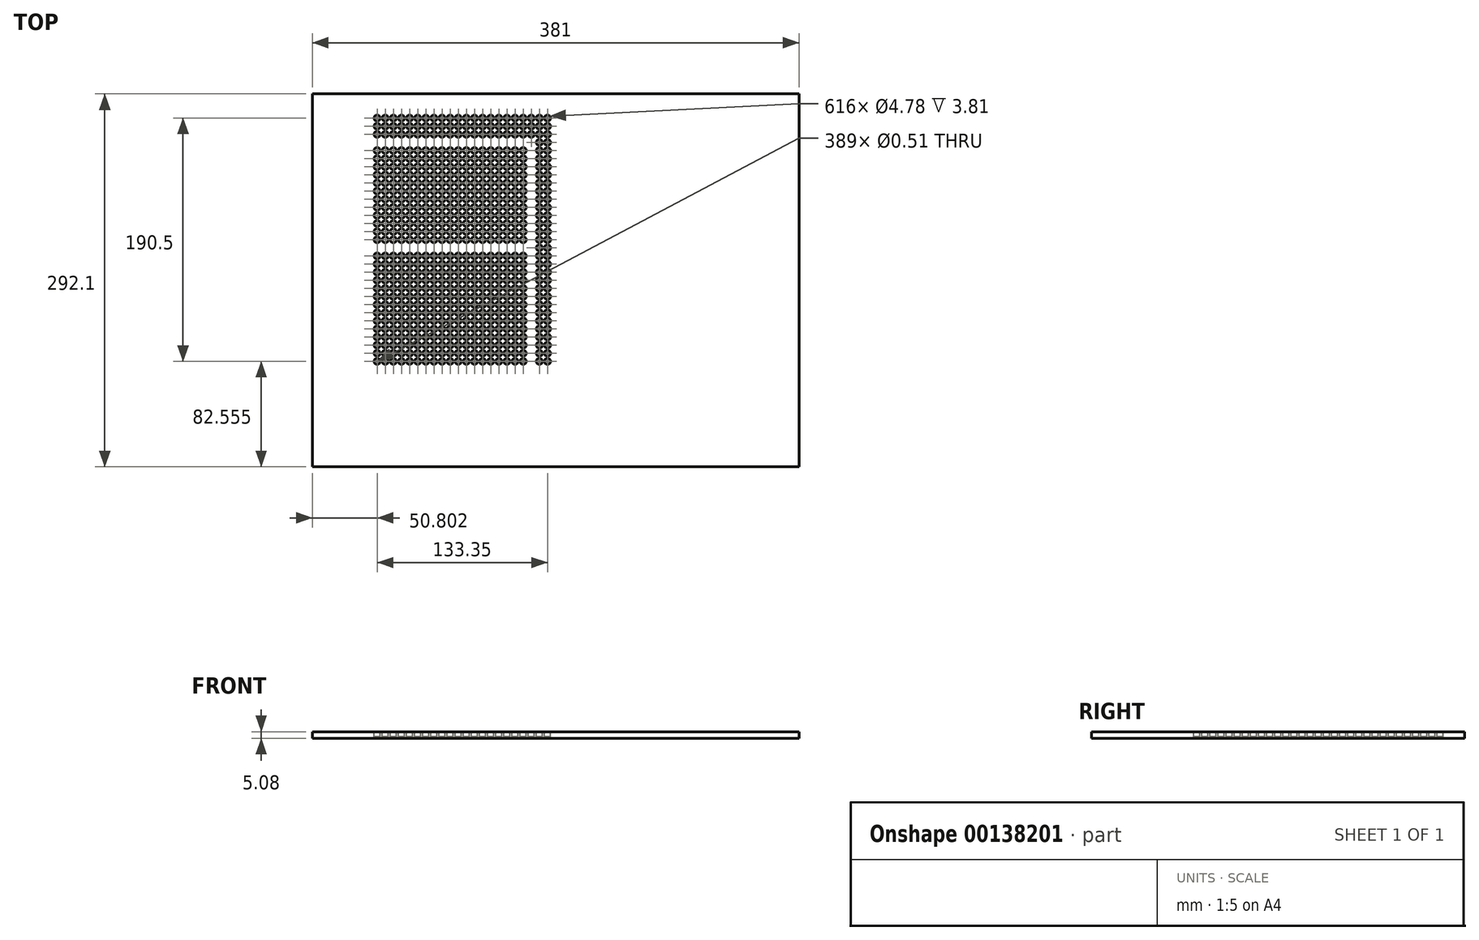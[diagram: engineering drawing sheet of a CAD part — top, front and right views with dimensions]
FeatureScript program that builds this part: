
annotation { "Feature Type Name" : "Feature", "Feature Type Description" : "" }
export const myFeature = defineFeature(function(context is Context, id is Id, definition is map)
    precondition{}
    {
        {
            var Q0;
            Q0=qCreatedBy(makeId("Top.planeOp"),FACE);
            var sketch = newSketch(context, id + "F0", { "sketchPlane" : qUnion([Q0])});
            skLineSegment(sketch, "E0.bottom", {"start": v(-148.53, -103.2) * mm, "end": v(232.47, -103.2) * mm});
            skLineSegment(sketch, "E0.top", {"start": v(-148.53, 188.9) * mm, "end": v(232.47, 188.9) * mm});
            skLineSegment(sketch, "E0.left", {"start": v(-148.53, -103.2) * mm, "end": v(-148.53, 188.9) * mm});
            skLineSegment(sketch, "E0.right", {"start": v(232.47, -103.2) * mm, "end": v(232.47, 188.9) * mm});
            skSolve(sketch);
        }
        {
            var Q0;
            Q0 = qSketchRegion(id + "F0", true);
            extrude(context, id + "F1", {"entities" : qUnion([Q0]), "depth" : 5.08 * mm});
        }
        {
            var Q0;
            Q0=makeQuery(id+"F1.opExtrude","CAP_FACE",FACE,{"disambiguationData":[OSD([sQuery(id+"F0.wireOp",EDGE,"E0.bottom"),sQuery(id+"F0.wireOp",EDGE,"E0.top"),sQuery(id+"F0.wireOp",EDGE,"E0.left"),sQuery(id+"F0.wireOp",EDGE,"E0.right")])],"isStart":false});
            var sketch = newSketch(context, id + "F2", { "sketchPlane" : qUnion([Q0])});
            skCircle(sketch, "E1", {"center": v(-97.73, -20.65) * mm, "radius": 2.39 * mm});
            skCircle(sketch, "E2.0.1.0", {"center": v(-97.73, -14.3) * mm, "radius": 2.39 * mm});
            skCircle(sketch, "E2.0.2.0", {"center": v(-97.73, -7.95) * mm, "radius": 2.39 * mm});
            skCircle(sketch, "E2.0.3.0", {"center": v(-97.73, -1.6) * mm, "radius": 2.39 * mm});
            skCircle(sketch, "E2.0.4.0", {"center": v(-97.73, 4.75) * mm, "radius": 2.39 * mm});
            skCircle(sketch, "E2.0.5.0", {"center": v(-97.73, 11.1) * mm, "radius": 2.39 * mm});
            skCircle(sketch, "E2.0.6.0", {"center": v(-97.73, 17.45) * mm, "radius": 2.39 * mm});
            skCircle(sketch, "E2.0.7.0", {"center": v(-97.73, 23.8) * mm, "radius": 2.39 * mm});
            skCircle(sketch, "E2.0.8.0", {"center": v(-97.73, 30.15) * mm, "radius": 2.39 * mm});
            skCircle(sketch, "E2.0.9.0", {"center": v(-97.73, 36.5) * mm, "radius": 2.39 * mm});
            skCircle(sketch, "E2.0.10.0", {"center": v(-97.73, 42.85) * mm, "radius": 2.39 * mm});
            skCircle(sketch, "E2.0.11.0", {"center": v(-97.73, 49.2) * mm, "radius": 2.39 * mm});
            skCircle(sketch, "E2.0.12.0", {"center": v(-97.73, 55.55) * mm, "radius": 2.39 * mm});
            skCircle(sketch, "E2.0.13.0", {"center": v(-97.73, 61.9) * mm, "radius": 2.39 * mm});
            skCircle(sketch, "E2.1.0.0", {"center": v(-91.38, -20.65) * mm, "radius": 2.39 * mm});
            skCircle(sketch, "E2.1.1.0", {"center": v(-91.38, -14.3) * mm, "radius": 2.39 * mm});
            skCircle(sketch, "E2.1.2.0", {"center": v(-91.38, -7.95) * mm, "radius": 2.39 * mm});
            skCircle(sketch, "E2.1.3.0", {"center": v(-91.38, -1.6) * mm, "radius": 2.39 * mm});
            skCircle(sketch, "E2.1.4.0", {"center": v(-91.38, 4.75) * mm, "radius": 2.39 * mm});
            skCircle(sketch, "E2.1.5.0", {"center": v(-91.38, 11.1) * mm, "radius": 2.39 * mm});
            skCircle(sketch, "E2.1.6.0", {"center": v(-91.38, 17.45) * mm, "radius": 2.39 * mm});
            skCircle(sketch, "E2.1.7.0", {"center": v(-91.38, 23.8) * mm, "radius": 2.39 * mm});
            skCircle(sketch, "E2.1.8.0", {"center": v(-91.38, 30.15) * mm, "radius": 2.39 * mm});
            skCircle(sketch, "E2.1.9.0", {"center": v(-91.38, 36.5) * mm, "radius": 2.39 * mm});
            skCircle(sketch, "E2.1.10.0", {"center": v(-91.38, 42.85) * mm, "radius": 2.39 * mm});
            skCircle(sketch, "E2.1.11.0", {"center": v(-91.38, 49.2) * mm, "radius": 2.39 * mm});
            skCircle(sketch, "E2.1.12.0", {"center": v(-91.38, 55.55) * mm, "radius": 2.39 * mm});
            skCircle(sketch, "E2.1.13.0", {"center": v(-91.38, 61.9) * mm, "radius": 2.39 * mm});
            skCircle(sketch, "E2.2.0.0", {"center": v(-85.03, -20.65) * mm, "radius": 2.39 * mm});
            skCircle(sketch, "E2.2.1.0", {"center": v(-85.03, -14.3) * mm, "radius": 2.39 * mm});
            skCircle(sketch, "E2.2.2.0", {"center": v(-85.03, -7.95) * mm, "radius": 2.39 * mm});
            skCircle(sketch, "E2.2.3.0", {"center": v(-85.03, -1.6) * mm, "radius": 2.39 * mm});
            skCircle(sketch, "E2.2.4.0", {"center": v(-85.03, 4.75) * mm, "radius": 2.39 * mm});
            skCircle(sketch, "E2.2.5.0", {"center": v(-85.03, 11.1) * mm, "radius": 2.39 * mm});
            skCircle(sketch, "E2.2.6.0", {"center": v(-85.03, 17.45) * mm, "radius": 2.39 * mm});
            skCircle(sketch, "E2.2.7.0", {"center": v(-85.03, 23.8) * mm, "radius": 2.39 * mm});
            skCircle(sketch, "E2.2.8.0", {"center": v(-85.03, 30.15) * mm, "radius": 2.39 * mm});
            skCircle(sketch, "E2.2.9.0", {"center": v(-85.03, 36.5) * mm, "radius": 2.39 * mm});
            skCircle(sketch, "E2.2.10.0", {"center": v(-85.03, 42.85) * mm, "radius": 2.39 * mm});
            skCircle(sketch, "E2.2.11.0", {"center": v(-85.03, 49.2) * mm, "radius": 2.39 * mm});
            skCircle(sketch, "E2.2.12.0", {"center": v(-85.03, 55.55) * mm, "radius": 2.39 * mm});
            skCircle(sketch, "E2.2.13.0", {"center": v(-85.03, 61.9) * mm, "radius": 2.39 * mm});
            skCircle(sketch, "E2.3.0.0", {"center": v(-78.68, -20.65) * mm, "radius": 2.39 * mm});
            skCircle(sketch, "E2.3.1.0", {"center": v(-78.68, -14.3) * mm, "radius": 2.39 * mm});
            skCircle(sketch, "E2.3.2.0", {"center": v(-78.68, -7.95) * mm, "radius": 2.39 * mm});
            skCircle(sketch, "E2.3.3.0", {"center": v(-78.68, -1.6) * mm, "radius": 2.39 * mm});
            skCircle(sketch, "E2.3.4.0", {"center": v(-78.68, 4.75) * mm, "radius": 2.39 * mm});
            skCircle(sketch, "E2.3.5.0", {"center": v(-78.68, 11.1) * mm, "radius": 2.39 * mm});
            skCircle(sketch, "E2.3.6.0", {"center": v(-78.68, 17.45) * mm, "radius": 2.39 * mm});
            skCircle(sketch, "E2.3.7.0", {"center": v(-78.68, 23.8) * mm, "radius": 2.39 * mm});
            skCircle(sketch, "E2.3.8.0", {"center": v(-78.68, 30.15) * mm, "radius": 2.39 * mm});
            skCircle(sketch, "E2.3.9.0", {"center": v(-78.68, 36.5) * mm, "radius": 2.39 * mm});
            skCircle(sketch, "E2.3.10.0", {"center": v(-78.68, 42.85) * mm, "radius": 2.39 * mm});
            skCircle(sketch, "E2.3.11.0", {"center": v(-78.68, 49.2) * mm, "radius": 2.39 * mm});
            skCircle(sketch, "E2.3.12.0", {"center": v(-78.68, 55.55) * mm, "radius": 2.39 * mm});
            skCircle(sketch, "E2.3.13.0", {"center": v(-78.68, 61.9) * mm, "radius": 2.39 * mm});
            skCircle(sketch, "E2.4.0.0", {"center": v(-72.33, -20.65) * mm, "radius": 2.39 * mm});
            skCircle(sketch, "E2.4.1.0", {"center": v(-72.33, -14.3) * mm, "radius": 2.39 * mm});
            skCircle(sketch, "E2.4.2.0", {"center": v(-72.33, -7.95) * mm, "radius": 2.39 * mm});
            skCircle(sketch, "E2.4.3.0", {"center": v(-72.33, -1.6) * mm, "radius": 2.39 * mm});
            skCircle(sketch, "E2.4.4.0", {"center": v(-72.33, 4.75) * mm, "radius": 2.39 * mm});
            skCircle(sketch, "E2.4.5.0", {"center": v(-72.33, 11.1) * mm, "radius": 2.39 * mm});
            skCircle(sketch, "E2.4.6.0", {"center": v(-72.33, 17.45) * mm, "radius": 2.39 * mm});
            skCircle(sketch, "E2.4.7.0", {"center": v(-72.33, 23.8) * mm, "radius": 2.39 * mm});
            skCircle(sketch, "E2.4.8.0", {"center": v(-72.33, 30.15) * mm, "radius": 2.39 * mm});
            skCircle(sketch, "E2.4.9.0", {"center": v(-72.33, 36.5) * mm, "radius": 2.39 * mm});
            skCircle(sketch, "E2.4.10.0", {"center": v(-72.33, 42.85) * mm, "radius": 2.39 * mm});
            skCircle(sketch, "E2.4.11.0", {"center": v(-72.33, 49.2) * mm, "radius": 2.39 * mm});
            skCircle(sketch, "E2.4.12.0", {"center": v(-72.33, 55.55) * mm, "radius": 2.39 * mm});
            skCircle(sketch, "E2.4.13.0", {"center": v(-72.33, 61.9) * mm, "radius": 2.39 * mm});
            skCircle(sketch, "E2.5.0.0", {"center": v(-65.98, -20.65) * mm, "radius": 2.39 * mm});
            skCircle(sketch, "E2.5.1.0", {"center": v(-65.98, -14.3) * mm, "radius": 2.39 * mm});
            skCircle(sketch, "E2.5.2.0", {"center": v(-65.98, -7.95) * mm, "radius": 2.39 * mm});
            skCircle(sketch, "E2.5.3.0", {"center": v(-65.98, -1.6) * mm, "radius": 2.39 * mm});
            skCircle(sketch, "E2.5.4.0", {"center": v(-65.98, 4.75) * mm, "radius": 2.39 * mm});
            skCircle(sketch, "E2.5.5.0", {"center": v(-65.98, 11.1) * mm, "radius": 2.39 * mm});
            skCircle(sketch, "E2.5.6.0", {"center": v(-65.98, 17.45) * mm, "radius": 2.39 * mm});
            skCircle(sketch, "E2.5.7.0", {"center": v(-65.98, 23.8) * mm, "radius": 2.39 * mm});
            skCircle(sketch, "E2.5.8.0", {"center": v(-65.98, 30.15) * mm, "radius": 2.39 * mm});
            skCircle(sketch, "E2.5.9.0", {"center": v(-65.98, 36.5) * mm, "radius": 2.39 * mm});
            skCircle(sketch, "E2.5.10.0", {"center": v(-65.98, 42.85) * mm, "radius": 2.39 * mm});
            skCircle(sketch, "E2.5.11.0", {"center": v(-65.98, 49.2) * mm, "radius": 2.39 * mm});
            skCircle(sketch, "E2.5.12.0", {"center": v(-65.98, 55.55) * mm, "radius": 2.39 * mm});
            skCircle(sketch, "E2.5.13.0", {"center": v(-65.98, 61.9) * mm, "radius": 2.39 * mm});
            skCircle(sketch, "E2.6.0.0", {"center": v(-59.63, -20.65) * mm, "radius": 2.39 * mm});
            skCircle(sketch, "E2.6.1.0", {"center": v(-59.63, -14.3) * mm, "radius": 2.39 * mm});
            skCircle(sketch, "E2.6.2.0", {"center": v(-59.63, -7.95) * mm, "radius": 2.39 * mm});
            skCircle(sketch, "E2.6.3.0", {"center": v(-59.63, -1.6) * mm, "radius": 2.39 * mm});
            skCircle(sketch, "E2.6.4.0", {"center": v(-59.63, 4.75) * mm, "radius": 2.39 * mm});
            skCircle(sketch, "E2.6.5.0", {"center": v(-59.63, 11.1) * mm, "radius": 2.39 * mm});
            skCircle(sketch, "E2.6.6.0", {"center": v(-59.63, 17.45) * mm, "radius": 2.39 * mm});
            skCircle(sketch, "E2.6.7.0", {"center": v(-59.63, 23.8) * mm, "radius": 2.39 * mm});
            skCircle(sketch, "E2.6.8.0", {"center": v(-59.63, 30.15) * mm, "radius": 2.39 * mm});
            skCircle(sketch, "E2.6.9.0", {"center": v(-59.63, 36.5) * mm, "radius": 2.39 * mm});
            skCircle(sketch, "E2.6.10.0", {"center": v(-59.63, 42.85) * mm, "radius": 2.39 * mm});
            skCircle(sketch, "E2.6.11.0", {"center": v(-59.63, 49.2) * mm, "radius": 2.39 * mm});
            skCircle(sketch, "E2.6.12.0", {"center": v(-59.63, 55.55) * mm, "radius": 2.39 * mm});
            skCircle(sketch, "E2.6.13.0", {"center": v(-59.63, 61.9) * mm, "radius": 2.39 * mm});
            skCircle(sketch, "E2.7.0.0", {"center": v(-53.28, -20.65) * mm, "radius": 2.39 * mm});
            skCircle(sketch, "E2.7.1.0", {"center": v(-53.28, -14.3) * mm, "radius": 2.39 * mm});
            skCircle(sketch, "E2.7.2.0", {"center": v(-53.28, -7.95) * mm, "radius": 2.39 * mm});
            skCircle(sketch, "E2.7.3.0", {"center": v(-53.28, -1.6) * mm, "radius": 2.39 * mm});
            skCircle(sketch, "E2.7.4.0", {"center": v(-53.28, 4.75) * mm, "radius": 2.39 * mm});
            skCircle(sketch, "E2.7.5.0", {"center": v(-53.28, 11.1) * mm, "radius": 2.39 * mm});
            skCircle(sketch, "E2.7.6.0", {"center": v(-53.28, 17.45) * mm, "radius": 2.39 * mm});
            skCircle(sketch, "E2.7.7.0", {"center": v(-53.28, 23.8) * mm, "radius": 2.39 * mm});
            skCircle(sketch, "E2.7.8.0", {"center": v(-53.28, 30.15) * mm, "radius": 2.39 * mm});
            skCircle(sketch, "E2.7.9.0", {"center": v(-53.28, 36.5) * mm, "radius": 2.39 * mm});
            skCircle(sketch, "E2.7.10.0", {"center": v(-53.28, 42.85) * mm, "radius": 2.39 * mm});
            skCircle(sketch, "E2.7.11.0", {"center": v(-53.28, 49.2) * mm, "radius": 2.39 * mm});
            skCircle(sketch, "E2.7.12.0", {"center": v(-53.28, 55.55) * mm, "radius": 2.39 * mm});
            skCircle(sketch, "E2.7.13.0", {"center": v(-53.28, 61.9) * mm, "radius": 2.39 * mm});
            skCircle(sketch, "E2.8.0.0", {"center": v(-46.93, -20.65) * mm, "radius": 2.39 * mm});
            skCircle(sketch, "E2.8.1.0", {"center": v(-46.93, -14.3) * mm, "radius": 2.39 * mm});
            skCircle(sketch, "E2.8.2.0", {"center": v(-46.93, -7.95) * mm, "radius": 2.39 * mm});
            skCircle(sketch, "E2.8.3.0", {"center": v(-46.93, -1.6) * mm, "radius": 2.39 * mm});
            skCircle(sketch, "E2.8.4.0", {"center": v(-46.93, 4.75) * mm, "radius": 2.39 * mm});
            skCircle(sketch, "E2.8.5.0", {"center": v(-46.93, 11.1) * mm, "radius": 2.39 * mm});
            skCircle(sketch, "E2.8.6.0", {"center": v(-46.93, 17.45) * mm, "radius": 2.39 * mm});
            skCircle(sketch, "E2.8.7.0", {"center": v(-46.93, 23.8) * mm, "radius": 2.39 * mm});
            skCircle(sketch, "E2.8.8.0", {"center": v(-46.93, 30.15) * mm, "radius": 2.39 * mm});
            skCircle(sketch, "E2.8.9.0", {"center": v(-46.93, 36.5) * mm, "radius": 2.39 * mm});
            skCircle(sketch, "E2.8.10.0", {"center": v(-46.93, 42.85) * mm, "radius": 2.39 * mm});
            skCircle(sketch, "E2.8.11.0", {"center": v(-46.93, 49.2) * mm, "radius": 2.39 * mm});
            skCircle(sketch, "E2.8.12.0", {"center": v(-46.93, 55.55) * mm, "radius": 2.39 * mm});
            skCircle(sketch, "E2.8.13.0", {"center": v(-46.93, 61.9) * mm, "radius": 2.39 * mm});
            skCircle(sketch, "E2.9.0.0", {"center": v(-40.58, -20.65) * mm, "radius": 2.39 * mm});
            skCircle(sketch, "E2.9.1.0", {"center": v(-40.58, -14.3) * mm, "radius": 2.39 * mm});
            skCircle(sketch, "E2.9.2.0", {"center": v(-40.58, -7.95) * mm, "radius": 2.39 * mm});
            skCircle(sketch, "E2.9.3.0", {"center": v(-40.58, -1.6) * mm, "radius": 2.39 * mm});
            skCircle(sketch, "E2.9.4.0", {"center": v(-40.58, 4.75) * mm, "radius": 2.39 * mm});
            skCircle(sketch, "E2.9.5.0", {"center": v(-40.58, 11.1) * mm, "radius": 2.39 * mm});
            skCircle(sketch, "E2.9.6.0", {"center": v(-40.58, 17.45) * mm, "radius": 2.39 * mm});
            skCircle(sketch, "E2.9.7.0", {"center": v(-40.58, 23.8) * mm, "radius": 2.39 * mm});
            skCircle(sketch, "E2.9.8.0", {"center": v(-40.58, 30.15) * mm, "radius": 2.39 * mm});
            skCircle(sketch, "E2.9.9.0", {"center": v(-40.58, 36.5) * mm, "radius": 2.39 * mm});
            skCircle(sketch, "E2.9.10.0", {"center": v(-40.58, 42.85) * mm, "radius": 2.39 * mm});
            skCircle(sketch, "E2.9.11.0", {"center": v(-40.58, 49.2) * mm, "radius": 2.39 * mm});
            skCircle(sketch, "E2.9.12.0", {"center": v(-40.58, 55.55) * mm, "radius": 2.39 * mm});
            skCircle(sketch, "E2.9.13.0", {"center": v(-40.58, 61.9) * mm, "radius": 2.39 * mm});
            skCircle(sketch, "E2.10.0.0", {"center": v(-34.23, -20.65) * mm, "radius": 2.39 * mm});
            skCircle(sketch, "E2.10.1.0", {"center": v(-34.23, -14.3) * mm, "radius": 2.39 * mm});
            skCircle(sketch, "E2.10.2.0", {"center": v(-34.23, -7.95) * mm, "radius": 2.39 * mm});
            skCircle(sketch, "E2.10.3.0", {"center": v(-34.23, -1.6) * mm, "radius": 2.39 * mm});
            skCircle(sketch, "E2.10.4.0", {"center": v(-34.23, 4.75) * mm, "radius": 2.39 * mm});
            skCircle(sketch, "E2.10.5.0", {"center": v(-34.23, 11.1) * mm, "radius": 2.39 * mm});
            skCircle(sketch, "E2.10.6.0", {"center": v(-34.23, 17.45) * mm, "radius": 2.39 * mm});
            skCircle(sketch, "E2.10.7.0", {"center": v(-34.23, 23.8) * mm, "radius": 2.39 * mm});
            skCircle(sketch, "E2.10.8.0", {"center": v(-34.23, 30.15) * mm, "radius": 2.39 * mm});
            skCircle(sketch, "E2.10.9.0", {"center": v(-34.23, 36.5) * mm, "radius": 2.39 * mm});
            skCircle(sketch, "E2.10.10.0", {"center": v(-34.23, 42.85) * mm, "radius": 2.39 * mm});
            skCircle(sketch, "E2.10.11.0", {"center": v(-34.23, 49.2) * mm, "radius": 2.39 * mm});
            skCircle(sketch, "E2.10.12.0", {"center": v(-34.23, 55.55) * mm, "radius": 2.39 * mm});
            skCircle(sketch, "E2.10.13.0", {"center": v(-34.23, 61.9) * mm, "radius": 2.39 * mm});
            skCircle(sketch, "E2.11.0.0", {"center": v(-27.88, -20.65) * mm, "radius": 2.39 * mm});
            skCircle(sketch, "E2.11.1.0", {"center": v(-27.88, -14.3) * mm, "radius": 2.39 * mm});
            skCircle(sketch, "E2.11.2.0", {"center": v(-27.88, -7.95) * mm, "radius": 2.39 * mm});
            skCircle(sketch, "E2.11.3.0", {"center": v(-27.88, -1.6) * mm, "radius": 2.39 * mm});
            skCircle(sketch, "E2.11.4.0", {"center": v(-27.88, 4.75) * mm, "radius": 2.39 * mm});
            skCircle(sketch, "E2.11.5.0", {"center": v(-27.88, 11.1) * mm, "radius": 2.39 * mm});
            skCircle(sketch, "E2.11.6.0", {"center": v(-27.88, 17.45) * mm, "radius": 2.39 * mm});
            skCircle(sketch, "E2.11.7.0", {"center": v(-27.88, 23.8) * mm, "radius": 2.39 * mm});
            skCircle(sketch, "E2.11.8.0", {"center": v(-27.88, 30.15) * mm, "radius": 2.39 * mm});
            skCircle(sketch, "E2.11.9.0", {"center": v(-27.88, 36.5) * mm, "radius": 2.39 * mm});
            skCircle(sketch, "E2.11.10.0", {"center": v(-27.88, 42.85) * mm, "radius": 2.39 * mm});
            skCircle(sketch, "E2.11.11.0", {"center": v(-27.88, 49.2) * mm, "radius": 2.39 * mm});
            skCircle(sketch, "E2.11.12.0", {"center": v(-27.88, 55.55) * mm, "radius": 2.39 * mm});
            skCircle(sketch, "E2.11.13.0", {"center": v(-27.88, 61.9) * mm, "radius": 2.39 * mm});
            skCircle(sketch, "E2.12.0.0", {"center": v(-21.53, -20.65) * mm, "radius": 2.39 * mm});
            skCircle(sketch, "E2.12.1.0", {"center": v(-21.53, -14.3) * mm, "radius": 2.39 * mm});
            skCircle(sketch, "E2.12.2.0", {"center": v(-21.53, -7.95) * mm, "radius": 2.39 * mm});
            skCircle(sketch, "E2.12.3.0", {"center": v(-21.53, -1.6) * mm, "radius": 2.39 * mm});
            skCircle(sketch, "E2.12.4.0", {"center": v(-21.53, 4.75) * mm, "radius": 2.39 * mm});
            skCircle(sketch, "E2.12.5.0", {"center": v(-21.53, 11.1) * mm, "radius": 2.39 * mm});
            skCircle(sketch, "E2.12.6.0", {"center": v(-21.53, 17.45) * mm, "radius": 2.39 * mm});
            skCircle(sketch, "E2.12.7.0", {"center": v(-21.53, 23.8) * mm, "radius": 2.39 * mm});
            skCircle(sketch, "E2.12.8.0", {"center": v(-21.53, 30.15) * mm, "radius": 2.39 * mm});
            skCircle(sketch, "E2.12.9.0", {"center": v(-21.53, 36.5) * mm, "radius": 2.39 * mm});
            skCircle(sketch, "E2.12.10.0", {"center": v(-21.53, 42.85) * mm, "radius": 2.39 * mm});
            skCircle(sketch, "E2.12.11.0", {"center": v(-21.53, 49.2) * mm, "radius": 2.39 * mm});
            skCircle(sketch, "E2.12.12.0", {"center": v(-21.53, 55.55) * mm, "radius": 2.39 * mm});
            skCircle(sketch, "E2.12.13.0", {"center": v(-21.53, 61.9) * mm, "radius": 2.39 * mm});
            skCircle(sketch, "E2.13.0.0", {"center": v(-15.18, -20.65) * mm, "radius": 2.39 * mm});
            skCircle(sketch, "E2.13.1.0", {"center": v(-15.18, -14.3) * mm, "radius": 2.39 * mm});
            skCircle(sketch, "E2.13.2.0", {"center": v(-15.18, -7.95) * mm, "radius": 2.39 * mm});
            skCircle(sketch, "E2.13.3.0", {"center": v(-15.18, -1.6) * mm, "radius": 2.39 * mm});
            skCircle(sketch, "E2.13.4.0", {"center": v(-15.18, 4.75) * mm, "radius": 2.39 * mm});
            skCircle(sketch, "E2.13.5.0", {"center": v(-15.18, 11.1) * mm, "radius": 2.39 * mm});
            skCircle(sketch, "E2.13.6.0", {"center": v(-15.18, 17.45) * mm, "radius": 2.39 * mm});
            skCircle(sketch, "E2.13.7.0", {"center": v(-15.18, 23.8) * mm, "radius": 2.39 * mm});
            skCircle(sketch, "E2.13.8.0", {"center": v(-15.18, 30.15) * mm, "radius": 2.39 * mm});
            skCircle(sketch, "E2.13.9.0", {"center": v(-15.18, 36.5) * mm, "radius": 2.39 * mm});
            skCircle(sketch, "E2.13.10.0", {"center": v(-15.18, 42.85) * mm, "radius": 2.39 * mm});
            skCircle(sketch, "E2.13.11.0", {"center": v(-15.18, 49.2) * mm, "radius": 2.39 * mm});
            skCircle(sketch, "E2.13.12.0", {"center": v(-15.18, 55.55) * mm, "radius": 2.39 * mm});
            skCircle(sketch, "E2.13.13.0", {"center": v(-15.18, 61.9) * mm, "radius": 2.39 * mm});
            skCircle(sketch, "E2.14.0.0", {"center": v(-8.83, -20.65) * mm, "radius": 2.39 * mm});
            skCircle(sketch, "E2.14.1.0", {"center": v(-8.83, -14.3) * mm, "radius": 2.39 * mm});
            skCircle(sketch, "E2.14.2.0", {"center": v(-8.83, -7.95) * mm, "radius": 2.39 * mm});
            skCircle(sketch, "E2.14.3.0", {"center": v(-8.83, -1.6) * mm, "radius": 2.39 * mm});
            skCircle(sketch, "E2.14.4.0", {"center": v(-8.83, 4.75) * mm, "radius": 2.39 * mm});
            skCircle(sketch, "E2.14.5.0", {"center": v(-8.83, 11.1) * mm, "radius": 2.39 * mm});
            skCircle(sketch, "E2.14.6.0", {"center": v(-8.83, 17.45) * mm, "radius": 2.39 * mm});
            skCircle(sketch, "E2.14.7.0", {"center": v(-8.83, 23.8) * mm, "radius": 2.39 * mm});
            skCircle(sketch, "E2.14.8.0", {"center": v(-8.83, 30.15) * mm, "radius": 2.39 * mm});
            skCircle(sketch, "E2.14.9.0", {"center": v(-8.83, 36.5) * mm, "radius": 2.39 * mm});
            skCircle(sketch, "E2.14.10.0", {"center": v(-8.83, 42.85) * mm, "radius": 2.39 * mm});
            skCircle(sketch, "E2.14.11.0", {"center": v(-8.83, 49.2) * mm, "radius": 2.39 * mm});
            skCircle(sketch, "E2.14.12.0", {"center": v(-8.83, 55.55) * mm, "radius": 2.39 * mm});
            skCircle(sketch, "E2.14.13.0", {"center": v(-8.83, 61.9) * mm, "radius": 2.39 * mm});
            skCircle(sketch, "E2.15.0.0", {"center": v(-2.48, -20.65) * mm, "radius": 2.39 * mm});
            skCircle(sketch, "E2.15.1.0", {"center": v(-2.48, -14.3) * mm, "radius": 2.39 * mm});
            skCircle(sketch, "E2.15.2.0", {"center": v(-2.48, -7.95) * mm, "radius": 2.39 * mm});
            skCircle(sketch, "E2.15.3.0", {"center": v(-2.48, -1.6) * mm, "radius": 2.39 * mm});
            skCircle(sketch, "E2.15.4.0", {"center": v(-2.48, 4.75) * mm, "radius": 2.39 * mm});
            skCircle(sketch, "E2.15.5.0", {"center": v(-2.48, 11.1) * mm, "radius": 2.39 * mm});
            skCircle(sketch, "E2.15.6.0", {"center": v(-2.48, 17.45) * mm, "radius": 2.39 * mm});
            skCircle(sketch, "E2.15.7.0", {"center": v(-2.48, 23.8) * mm, "radius": 2.39 * mm});
            skCircle(sketch, "E2.15.8.0", {"center": v(-2.48, 30.15) * mm, "radius": 2.39 * mm});
            skCircle(sketch, "E2.15.9.0", {"center": v(-2.48, 36.5) * mm, "radius": 2.39 * mm});
            skCircle(sketch, "E2.15.10.0", {"center": v(-2.48, 42.85) * mm, "radius": 2.39 * mm});
            skCircle(sketch, "E2.15.11.0", {"center": v(-2.48, 49.2) * mm, "radius": 2.39 * mm});
            skCircle(sketch, "E2.15.12.0", {"center": v(-2.48, 55.55) * mm, "radius": 2.39 * mm});
            skCircle(sketch, "E2.15.13.0", {"center": v(-2.48, 61.9) * mm, "radius": 2.39 * mm});
            skCircle(sketch, "E2.16.0.0", {"center": v(3.87, -20.65) * mm, "radius": 2.39 * mm});
            skCircle(sketch, "E2.16.1.0", {"center": v(3.87, -14.3) * mm, "radius": 2.39 * mm});
            skCircle(sketch, "E2.16.2.0", {"center": v(3.87, -7.95) * mm, "radius": 2.39 * mm});
            skCircle(sketch, "E2.16.3.0", {"center": v(3.87, -1.6) * mm, "radius": 2.39 * mm});
            skCircle(sketch, "E2.16.4.0", {"center": v(3.87, 4.75) * mm, "radius": 2.39 * mm});
            skCircle(sketch, "E2.16.5.0", {"center": v(3.87, 11.1) * mm, "radius": 2.39 * mm});
            skCircle(sketch, "E2.16.6.0", {"center": v(3.87, 17.45) * mm, "radius": 2.39 * mm});
            skCircle(sketch, "E2.16.7.0", {"center": v(3.87, 23.8) * mm, "radius": 2.39 * mm});
            skCircle(sketch, "E2.16.8.0", {"center": v(3.87, 30.15) * mm, "radius": 2.39 * mm});
            skCircle(sketch, "E2.16.9.0", {"center": v(3.87, 36.5) * mm, "radius": 2.39 * mm});
            skCircle(sketch, "E2.16.10.0", {"center": v(3.87, 42.85) * mm, "radius": 2.39 * mm});
            skCircle(sketch, "E2.16.11.0", {"center": v(3.87, 49.2) * mm, "radius": 2.39 * mm});
            skCircle(sketch, "E2.16.12.0", {"center": v(3.87, 55.55) * mm, "radius": 2.39 * mm});
            skCircle(sketch, "E2.16.13.0", {"center": v(3.87, 61.9) * mm, "radius": 2.39 * mm});
            skCircle(sketch, "E2.17.0.0", {"center": v(10.22, -20.65) * mm, "radius": 2.39 * mm});
            skCircle(sketch, "E2.17.1.0", {"center": v(10.22, -14.3) * mm, "radius": 2.39 * mm});
            skCircle(sketch, "E2.17.2.0", {"center": v(10.22, -7.95) * mm, "radius": 2.39 * mm});
            skCircle(sketch, "E2.17.3.0", {"center": v(10.22, -1.6) * mm, "radius": 2.39 * mm});
            skCircle(sketch, "E2.17.4.0", {"center": v(10.22, 4.75) * mm, "radius": 2.39 * mm});
            skCircle(sketch, "E2.17.5.0", {"center": v(10.22, 11.1) * mm, "radius": 2.39 * mm});
            skCircle(sketch, "E2.17.6.0", {"center": v(10.22, 17.45) * mm, "radius": 2.39 * mm});
            skCircle(sketch, "E2.17.7.0", {"center": v(10.22, 23.8) * mm, "radius": 2.39 * mm});
            skCircle(sketch, "E2.17.8.0", {"center": v(10.22, 30.15) * mm, "radius": 2.39 * mm});
            skCircle(sketch, "E2.17.9.0", {"center": v(10.22, 36.5) * mm, "radius": 2.39 * mm});
            skCircle(sketch, "E2.17.10.0", {"center": v(10.22, 42.85) * mm, "radius": 2.39 * mm});
            skCircle(sketch, "E2.17.11.0", {"center": v(10.22, 49.2) * mm, "radius": 2.39 * mm});
            skCircle(sketch, "E2.17.12.0", {"center": v(10.22, 55.55) * mm, "radius": 2.39 * mm});
            skCircle(sketch, "E2.17.13.0", {"center": v(10.22, 61.9) * mm, "radius": 2.39 * mm});
            skCircle(sketch, "E2.18.0.0", {"center": v(16.57, -20.65) * mm, "radius": 2.39 * mm});
            skCircle(sketch, "E2.18.1.0", {"center": v(16.57, -14.3) * mm, "radius": 2.39 * mm});
            skCircle(sketch, "E2.18.2.0", {"center": v(16.57, -7.95) * mm, "radius": 2.39 * mm});
            skCircle(sketch, "E2.18.3.0", {"center": v(16.57, -1.6) * mm, "radius": 2.39 * mm});
            skCircle(sketch, "E2.18.4.0", {"center": v(16.57, 4.75) * mm, "radius": 2.39 * mm});
            skCircle(sketch, "E2.18.5.0", {"center": v(16.57, 11.1) * mm, "radius": 2.39 * mm});
            skCircle(sketch, "E2.18.6.0", {"center": v(16.57, 17.45) * mm, "radius": 2.39 * mm});
            skCircle(sketch, "E2.18.7.0", {"center": v(16.57, 23.8) * mm, "radius": 2.39 * mm});
            skCircle(sketch, "E2.18.8.0", {"center": v(16.57, 30.15) * mm, "radius": 2.39 * mm});
            skCircle(sketch, "E2.18.9.0", {"center": v(16.57, 36.5) * mm, "radius": 2.39 * mm});
            skCircle(sketch, "E2.18.10.0", {"center": v(16.57, 42.85) * mm, "radius": 2.39 * mm});
            skCircle(sketch, "E2.18.11.0", {"center": v(16.57, 49.2) * mm, "radius": 2.39 * mm});
            skCircle(sketch, "E2.18.12.0", {"center": v(16.57, 55.55) * mm, "radius": 2.39 * mm});
            skCircle(sketch, "E2.18.13.0", {"center": v(16.57, 61.9) * mm, "radius": 2.39 * mm});
            skLineSegment(sketch, "E2.direction1", {"start": v(-97.73, -20.65) * mm, "end": v(-91.38, -20.65) * mm, "construction": true});
            skLineSegment(sketch, "E2.direction2", {"start": v(-97.73, -20.65) * mm, "end": v(-97.73, -14.3) * mm, "construction": true});
            skCircle(sketch, "E3", {"center": v(-97.73, 74.6) * mm, "radius": 2.39 * mm});
            skCircle(sketch, "E4.0.1.0", {"center": v(-97.73, 80.95) * mm, "radius": 2.39 * mm});
            skCircle(sketch, "E4.0.2.0", {"center": v(-97.73, 87.3) * mm, "radius": 2.39 * mm});
            skCircle(sketch, "E4.0.3.0", {"center": v(-97.73, 93.65) * mm, "radius": 2.39 * mm});
            skCircle(sketch, "E4.0.4.0", {"center": v(-97.73, 100) * mm, "radius": 2.39 * mm});
            skCircle(sketch, "E4.0.5.0", {"center": v(-97.73, 106.35) * mm, "radius": 2.39 * mm});
            skCircle(sketch, "E4.0.6.0", {"center": v(-97.73, 112.7) * mm, "radius": 2.39 * mm});
            skCircle(sketch, "E4.0.7.0", {"center": v(-97.73, 119.05) * mm, "radius": 2.39 * mm});
            skCircle(sketch, "E4.0.8.0", {"center": v(-97.73, 125.4) * mm, "radius": 2.39 * mm});
            skCircle(sketch, "E4.0.9.0", {"center": v(-97.73, 131.75) * mm, "radius": 2.39 * mm});
            skCircle(sketch, "E4.0.10.0", {"center": v(-97.73, 138.1) * mm, "radius": 2.39 * mm});
            skCircle(sketch, "E4.0.11.0", {"center": v(-97.73, 144.45) * mm, "radius": 2.39 * mm});
            skCircle(sketch, "E4.1.0.0", {"center": v(-91.38, 74.6) * mm, "radius": 2.39 * mm});
            skCircle(sketch, "E4.1.1.0", {"center": v(-91.38, 80.95) * mm, "radius": 2.39 * mm});
            skCircle(sketch, "E4.1.2.0", {"center": v(-91.38, 87.3) * mm, "radius": 2.39 * mm});
            skCircle(sketch, "E4.1.3.0", {"center": v(-91.38, 93.65) * mm, "radius": 2.39 * mm});
            skCircle(sketch, "E4.1.4.0", {"center": v(-91.38, 100) * mm, "radius": 2.39 * mm});
            skCircle(sketch, "E4.1.5.0", {"center": v(-91.38, 106.35) * mm, "radius": 2.39 * mm});
            skCircle(sketch, "E4.1.6.0", {"center": v(-91.38, 112.7) * mm, "radius": 2.39 * mm});
            skCircle(sketch, "E4.1.7.0", {"center": v(-91.38, 119.05) * mm, "radius": 2.39 * mm});
            skCircle(sketch, "E4.1.8.0", {"center": v(-91.38, 125.4) * mm, "radius": 2.39 * mm});
            skCircle(sketch, "E4.1.9.0", {"center": v(-91.38, 131.75) * mm, "radius": 2.39 * mm});
            skCircle(sketch, "E4.1.10.0", {"center": v(-91.38, 138.1) * mm, "radius": 2.39 * mm});
            skCircle(sketch, "E4.1.11.0", {"center": v(-91.38, 144.45) * mm, "radius": 2.39 * mm});
            skCircle(sketch, "E4.2.0.0", {"center": v(-85.03, 74.6) * mm, "radius": 2.39 * mm});
            skCircle(sketch, "E4.2.1.0", {"center": v(-85.03, 80.95) * mm, "radius": 2.39 * mm});
            skCircle(sketch, "E4.2.2.0", {"center": v(-85.03, 87.3) * mm, "radius": 2.39 * mm});
            skCircle(sketch, "E4.2.3.0", {"center": v(-85.03, 93.65) * mm, "radius": 2.39 * mm});
            skCircle(sketch, "E4.2.4.0", {"center": v(-85.03, 100) * mm, "radius": 2.39 * mm});
            skCircle(sketch, "E4.2.5.0", {"center": v(-85.03, 106.35) * mm, "radius": 2.39 * mm});
            skCircle(sketch, "E4.2.6.0", {"center": v(-85.03, 112.7) * mm, "radius": 2.39 * mm});
            skCircle(sketch, "E4.2.7.0", {"center": v(-85.03, 119.05) * mm, "radius": 2.39 * mm});
            skCircle(sketch, "E4.2.8.0", {"center": v(-85.03, 125.4) * mm, "radius": 2.39 * mm});
            skCircle(sketch, "E4.2.9.0", {"center": v(-85.03, 131.75) * mm, "radius": 2.39 * mm});
            skCircle(sketch, "E4.2.10.0", {"center": v(-85.03, 138.1) * mm, "radius": 2.39 * mm});
            skCircle(sketch, "E4.2.11.0", {"center": v(-85.03, 144.45) * mm, "radius": 2.39 * mm});
            skCircle(sketch, "E4.3.0.0", {"center": v(-78.68, 74.6) * mm, "radius": 2.39 * mm});
            skCircle(sketch, "E4.3.1.0", {"center": v(-78.68, 80.95) * mm, "radius": 2.39 * mm});
            skCircle(sketch, "E4.3.2.0", {"center": v(-78.68, 87.3) * mm, "radius": 2.39 * mm});
            skCircle(sketch, "E4.3.3.0", {"center": v(-78.68, 93.65) * mm, "radius": 2.39 * mm});
            skCircle(sketch, "E4.3.4.0", {"center": v(-78.68, 100) * mm, "radius": 2.39 * mm});
            skCircle(sketch, "E4.3.5.0", {"center": v(-78.68, 106.35) * mm, "radius": 2.39 * mm});
            skCircle(sketch, "E4.3.6.0", {"center": v(-78.68, 112.7) * mm, "radius": 2.39 * mm});
            skCircle(sketch, "E4.3.7.0", {"center": v(-78.68, 119.05) * mm, "radius": 2.39 * mm});
            skCircle(sketch, "E4.3.8.0", {"center": v(-78.68, 125.4) * mm, "radius": 2.39 * mm});
            skCircle(sketch, "E4.3.9.0", {"center": v(-78.68, 131.75) * mm, "radius": 2.39 * mm});
            skCircle(sketch, "E4.3.10.0", {"center": v(-78.68, 138.1) * mm, "radius": 2.39 * mm});
            skCircle(sketch, "E4.3.11.0", {"center": v(-78.68, 144.45) * mm, "radius": 2.39 * mm});
            skCircle(sketch, "E4.4.0.0", {"center": v(-72.33, 74.6) * mm, "radius": 2.39 * mm});
            skCircle(sketch, "E4.4.1.0", {"center": v(-72.33, 80.95) * mm, "radius": 2.39 * mm});
            skCircle(sketch, "E4.4.2.0", {"center": v(-72.33, 87.3) * mm, "radius": 2.39 * mm});
            skCircle(sketch, "E4.4.3.0", {"center": v(-72.33, 93.65) * mm, "radius": 2.39 * mm});
            skCircle(sketch, "E4.4.4.0", {"center": v(-72.33, 100) * mm, "radius": 2.39 * mm});
            skCircle(sketch, "E4.4.5.0", {"center": v(-72.33, 106.35) * mm, "radius": 2.39 * mm});
            skCircle(sketch, "E4.4.6.0", {"center": v(-72.33, 112.7) * mm, "radius": 2.39 * mm});
            skCircle(sketch, "E4.4.7.0", {"center": v(-72.33, 119.05) * mm, "radius": 2.39 * mm});
            skCircle(sketch, "E4.4.8.0", {"center": v(-72.33, 125.4) * mm, "radius": 2.39 * mm});
            skCircle(sketch, "E4.4.9.0", {"center": v(-72.33, 131.75) * mm, "radius": 2.39 * mm});
            skCircle(sketch, "E4.4.10.0", {"center": v(-72.33, 138.1) * mm, "radius": 2.39 * mm});
            skCircle(sketch, "E4.4.11.0", {"center": v(-72.33, 144.45) * mm, "radius": 2.39 * mm});
            skCircle(sketch, "E4.5.0.0", {"center": v(-65.98, 74.6) * mm, "radius": 2.39 * mm});
            skCircle(sketch, "E4.5.1.0", {"center": v(-65.98, 80.95) * mm, "radius": 2.39 * mm});
            skCircle(sketch, "E4.5.2.0", {"center": v(-65.98, 87.3) * mm, "radius": 2.39 * mm});
            skCircle(sketch, "E4.5.3.0", {"center": v(-65.98, 93.65) * mm, "radius": 2.39 * mm});
            skCircle(sketch, "E4.5.4.0", {"center": v(-65.98, 100) * mm, "radius": 2.39 * mm});
            skCircle(sketch, "E4.5.5.0", {"center": v(-65.98, 106.35) * mm, "radius": 2.39 * mm});
            skCircle(sketch, "E4.5.6.0", {"center": v(-65.98, 112.7) * mm, "radius": 2.39 * mm});
            skCircle(sketch, "E4.5.7.0", {"center": v(-65.98, 119.05) * mm, "radius": 2.39 * mm});
            skCircle(sketch, "E4.5.8.0", {"center": v(-65.98, 125.4) * mm, "radius": 2.39 * mm});
            skCircle(sketch, "E4.5.9.0", {"center": v(-65.98, 131.75) * mm, "radius": 2.39 * mm});
            skCircle(sketch, "E4.5.10.0", {"center": v(-65.98, 138.1) * mm, "radius": 2.39 * mm});
            skCircle(sketch, "E4.5.11.0", {"center": v(-65.98, 144.45) * mm, "radius": 2.39 * mm});
            skCircle(sketch, "E4.6.0.0", {"center": v(-59.63, 74.6) * mm, "radius": 2.39 * mm});
            skCircle(sketch, "E4.6.1.0", {"center": v(-59.63, 80.95) * mm, "radius": 2.39 * mm});
            skCircle(sketch, "E4.6.2.0", {"center": v(-59.63, 87.3) * mm, "radius": 2.39 * mm});
            skCircle(sketch, "E4.6.3.0", {"center": v(-59.63, 93.65) * mm, "radius": 2.39 * mm});
            skCircle(sketch, "E4.6.4.0", {"center": v(-59.63, 100) * mm, "radius": 2.39 * mm});
            skCircle(sketch, "E4.6.5.0", {"center": v(-59.63, 106.35) * mm, "radius": 2.39 * mm});
            skCircle(sketch, "E4.6.6.0", {"center": v(-59.63, 112.7) * mm, "radius": 2.39 * mm});
            skCircle(sketch, "E4.6.7.0", {"center": v(-59.63, 119.05) * mm, "radius": 2.39 * mm});
            skCircle(sketch, "E4.6.8.0", {"center": v(-59.63, 125.4) * mm, "radius": 2.39 * mm});
            skCircle(sketch, "E4.6.9.0", {"center": v(-59.63, 131.75) * mm, "radius": 2.39 * mm});
            skCircle(sketch, "E4.6.10.0", {"center": v(-59.63, 138.1) * mm, "radius": 2.39 * mm});
            skCircle(sketch, "E4.6.11.0", {"center": v(-59.63, 144.45) * mm, "radius": 2.39 * mm});
            skCircle(sketch, "E4.7.0.0", {"center": v(-53.28, 74.6) * mm, "radius": 2.39 * mm});
            skCircle(sketch, "E4.7.1.0", {"center": v(-53.28, 80.95) * mm, "radius": 2.39 * mm});
            skCircle(sketch, "E4.7.2.0", {"center": v(-53.28, 87.3) * mm, "radius": 2.39 * mm});
            skCircle(sketch, "E4.7.3.0", {"center": v(-53.28, 93.65) * mm, "radius": 2.39 * mm});
            skCircle(sketch, "E4.7.4.0", {"center": v(-53.28, 100) * mm, "radius": 2.39 * mm});
            skCircle(sketch, "E4.7.5.0", {"center": v(-53.28, 106.35) * mm, "radius": 2.39 * mm});
            skCircle(sketch, "E4.7.6.0", {"center": v(-53.28, 112.7) * mm, "radius": 2.39 * mm});
            skCircle(sketch, "E4.7.7.0", {"center": v(-53.28, 119.05) * mm, "radius": 2.39 * mm});
            skCircle(sketch, "E4.7.8.0", {"center": v(-53.28, 125.4) * mm, "radius": 2.39 * mm});
            skCircle(sketch, "E4.7.9.0", {"center": v(-53.28, 131.75) * mm, "radius": 2.39 * mm});
            skCircle(sketch, "E4.7.10.0", {"center": v(-53.28, 138.1) * mm, "radius": 2.39 * mm});
            skCircle(sketch, "E4.7.11.0", {"center": v(-53.28, 144.45) * mm, "radius": 2.39 * mm});
            skCircle(sketch, "E4.8.0.0", {"center": v(-46.93, 74.6) * mm, "radius": 2.39 * mm});
            skCircle(sketch, "E4.8.1.0", {"center": v(-46.93, 80.95) * mm, "radius": 2.39 * mm});
            skCircle(sketch, "E4.8.2.0", {"center": v(-46.93, 87.3) * mm, "radius": 2.39 * mm});
            skCircle(sketch, "E4.8.3.0", {"center": v(-46.93, 93.65) * mm, "radius": 2.39 * mm});
            skCircle(sketch, "E4.8.4.0", {"center": v(-46.93, 100) * mm, "radius": 2.39 * mm});
            skCircle(sketch, "E4.8.5.0", {"center": v(-46.93, 106.35) * mm, "radius": 2.39 * mm});
            skCircle(sketch, "E4.8.6.0", {"center": v(-46.93, 112.7) * mm, "radius": 2.39 * mm});
            skCircle(sketch, "E4.8.7.0", {"center": v(-46.93, 119.05) * mm, "radius": 2.39 * mm});
            skCircle(sketch, "E4.8.8.0", {"center": v(-46.93, 125.4) * mm, "radius": 2.39 * mm});
            skCircle(sketch, "E4.8.9.0", {"center": v(-46.93, 131.75) * mm, "radius": 2.39 * mm});
            skCircle(sketch, "E4.8.10.0", {"center": v(-46.93, 138.1) * mm, "radius": 2.39 * mm});
            skCircle(sketch, "E4.8.11.0", {"center": v(-46.93, 144.45) * mm, "radius": 2.39 * mm});
            skCircle(sketch, "E4.9.0.0", {"center": v(-40.58, 74.6) * mm, "radius": 2.39 * mm});
            skCircle(sketch, "E4.9.1.0", {"center": v(-40.58, 80.95) * mm, "radius": 2.39 * mm});
            skCircle(sketch, "E4.9.2.0", {"center": v(-40.58, 87.3) * mm, "radius": 2.39 * mm});
            skCircle(sketch, "E4.9.3.0", {"center": v(-40.58, 93.65) * mm, "radius": 2.39 * mm});
            skCircle(sketch, "E4.9.4.0", {"center": v(-40.58, 100) * mm, "radius": 2.39 * mm});
            skCircle(sketch, "E4.9.5.0", {"center": v(-40.58, 106.35) * mm, "radius": 2.39 * mm});
            skCircle(sketch, "E4.9.6.0", {"center": v(-40.58, 112.7) * mm, "radius": 2.39 * mm});
            skCircle(sketch, "E4.9.7.0", {"center": v(-40.58, 119.05) * mm, "radius": 2.39 * mm});
            skCircle(sketch, "E4.9.8.0", {"center": v(-40.58, 125.4) * mm, "radius": 2.39 * mm});
            skCircle(sketch, "E4.9.9.0", {"center": v(-40.58, 131.75) * mm, "radius": 2.39 * mm});
            skCircle(sketch, "E4.9.10.0", {"center": v(-40.58, 138.1) * mm, "radius": 2.39 * mm});
            skCircle(sketch, "E4.9.11.0", {"center": v(-40.58, 144.45) * mm, "radius": 2.39 * mm});
            skCircle(sketch, "E4.10.0.0", {"center": v(-34.23, 74.6) * mm, "radius": 2.39 * mm});
            skCircle(sketch, "E4.10.1.0", {"center": v(-34.23, 80.95) * mm, "radius": 2.39 * mm});
            skCircle(sketch, "E4.10.2.0", {"center": v(-34.23, 87.3) * mm, "radius": 2.39 * mm});
            skCircle(sketch, "E4.10.3.0", {"center": v(-34.23, 93.65) * mm, "radius": 2.39 * mm});
            skCircle(sketch, "E4.10.4.0", {"center": v(-34.23, 100) * mm, "radius": 2.39 * mm});
            skCircle(sketch, "E4.10.5.0", {"center": v(-34.23, 106.35) * mm, "radius": 2.39 * mm});
            skCircle(sketch, "E4.10.6.0", {"center": v(-34.23, 112.7) * mm, "radius": 2.39 * mm});
            skCircle(sketch, "E4.10.7.0", {"center": v(-34.23, 119.05) * mm, "radius": 2.39 * mm});
            skCircle(sketch, "E4.10.8.0", {"center": v(-34.23, 125.4) * mm, "radius": 2.39 * mm});
            skCircle(sketch, "E4.10.9.0", {"center": v(-34.23, 131.75) * mm, "radius": 2.39 * mm});
            skCircle(sketch, "E4.10.10.0", {"center": v(-34.23, 138.1) * mm, "radius": 2.39 * mm});
            skCircle(sketch, "E4.10.11.0", {"center": v(-34.23, 144.45) * mm, "radius": 2.39 * mm});
            skCircle(sketch, "E4.11.0.0", {"center": v(-27.88, 74.6) * mm, "radius": 2.39 * mm});
            skCircle(sketch, "E4.11.1.0", {"center": v(-27.88, 80.95) * mm, "radius": 2.39 * mm});
            skCircle(sketch, "E4.11.2.0", {"center": v(-27.88, 87.3) * mm, "radius": 2.39 * mm});
            skCircle(sketch, "E4.11.3.0", {"center": v(-27.88, 93.65) * mm, "radius": 2.39 * mm});
            skCircle(sketch, "E4.11.4.0", {"center": v(-27.88, 100) * mm, "radius": 2.39 * mm});
            skCircle(sketch, "E4.11.5.0", {"center": v(-27.88, 106.35) * mm, "radius": 2.39 * mm});
            skCircle(sketch, "E4.11.6.0", {"center": v(-27.88, 112.7) * mm, "radius": 2.39 * mm});
            skCircle(sketch, "E4.11.7.0", {"center": v(-27.88, 119.05) * mm, "radius": 2.39 * mm});
            skCircle(sketch, "E4.11.8.0", {"center": v(-27.88, 125.4) * mm, "radius": 2.39 * mm});
            skCircle(sketch, "E4.11.9.0", {"center": v(-27.88, 131.75) * mm, "radius": 2.39 * mm});
            skCircle(sketch, "E4.11.10.0", {"center": v(-27.88, 138.1) * mm, "radius": 2.39 * mm});
            skCircle(sketch, "E4.11.11.0", {"center": v(-27.88, 144.45) * mm, "radius": 2.39 * mm});
            skCircle(sketch, "E4.12.0.0", {"center": v(-21.53, 74.6) * mm, "radius": 2.39 * mm});
            skCircle(sketch, "E4.12.1.0", {"center": v(-21.53, 80.95) * mm, "radius": 2.39 * mm});
            skCircle(sketch, "E4.12.2.0", {"center": v(-21.53, 87.3) * mm, "radius": 2.39 * mm});
            skCircle(sketch, "E4.12.3.0", {"center": v(-21.53, 93.65) * mm, "radius": 2.39 * mm});
            skCircle(sketch, "E4.12.4.0", {"center": v(-21.53, 100) * mm, "radius": 2.39 * mm});
            skCircle(sketch, "E4.12.5.0", {"center": v(-21.53, 106.35) * mm, "radius": 2.39 * mm});
            skCircle(sketch, "E4.12.6.0", {"center": v(-21.53, 112.7) * mm, "radius": 2.39 * mm});
            skCircle(sketch, "E4.12.7.0", {"center": v(-21.53, 119.05) * mm, "radius": 2.39 * mm});
            skCircle(sketch, "E4.12.8.0", {"center": v(-21.53, 125.4) * mm, "radius": 2.39 * mm});
            skCircle(sketch, "E4.12.9.0", {"center": v(-21.53, 131.75) * mm, "radius": 2.39 * mm});
            skCircle(sketch, "E4.12.10.0", {"center": v(-21.53, 138.1) * mm, "radius": 2.39 * mm});
            skCircle(sketch, "E4.12.11.0", {"center": v(-21.53, 144.45) * mm, "radius": 2.39 * mm});
            skCircle(sketch, "E4.13.0.0", {"center": v(-15.18, 74.6) * mm, "radius": 2.39 * mm});
            skCircle(sketch, "E4.13.1.0", {"center": v(-15.18, 80.95) * mm, "radius": 2.39 * mm});
            skCircle(sketch, "E4.13.2.0", {"center": v(-15.18, 87.3) * mm, "radius": 2.39 * mm});
            skCircle(sketch, "E4.13.3.0", {"center": v(-15.18, 93.65) * mm, "radius": 2.39 * mm});
            skCircle(sketch, "E4.13.4.0", {"center": v(-15.18, 100) * mm, "radius": 2.39 * mm});
            skCircle(sketch, "E4.13.5.0", {"center": v(-15.18, 106.35) * mm, "radius": 2.39 * mm});
            skCircle(sketch, "E4.13.6.0", {"center": v(-15.18, 112.7) * mm, "radius": 2.39 * mm});
            skCircle(sketch, "E4.13.7.0", {"center": v(-15.18, 119.05) * mm, "radius": 2.39 * mm});
            skCircle(sketch, "E4.13.8.0", {"center": v(-15.18, 125.4) * mm, "radius": 2.39 * mm});
            skCircle(sketch, "E4.13.9.0", {"center": v(-15.18, 131.75) * mm, "radius": 2.39 * mm});
            skCircle(sketch, "E4.13.10.0", {"center": v(-15.18, 138.1) * mm, "radius": 2.39 * mm});
            skCircle(sketch, "E4.13.11.0", {"center": v(-15.18, 144.45) * mm, "radius": 2.39 * mm});
            skCircle(sketch, "E4.14.0.0", {"center": v(-8.83, 74.6) * mm, "radius": 2.39 * mm});
            skCircle(sketch, "E4.14.1.0", {"center": v(-8.83, 80.95) * mm, "radius": 2.39 * mm});
            skCircle(sketch, "E4.14.2.0", {"center": v(-8.83, 87.3) * mm, "radius": 2.39 * mm});
            skCircle(sketch, "E4.14.3.0", {"center": v(-8.83, 93.65) * mm, "radius": 2.39 * mm});
            skCircle(sketch, "E4.14.4.0", {"center": v(-8.83, 100) * mm, "radius": 2.39 * mm});
            skCircle(sketch, "E4.14.5.0", {"center": v(-8.83, 106.35) * mm, "radius": 2.39 * mm});
            skCircle(sketch, "E4.14.6.0", {"center": v(-8.83, 112.7) * mm, "radius": 2.39 * mm});
            skCircle(sketch, "E4.14.7.0", {"center": v(-8.83, 119.05) * mm, "radius": 2.39 * mm});
            skCircle(sketch, "E4.14.8.0", {"center": v(-8.83, 125.4) * mm, "radius": 2.39 * mm});
            skCircle(sketch, "E4.14.9.0", {"center": v(-8.83, 131.75) * mm, "radius": 2.39 * mm});
            skCircle(sketch, "E4.14.10.0", {"center": v(-8.83, 138.1) * mm, "radius": 2.39 * mm});
            skCircle(sketch, "E4.14.11.0", {"center": v(-8.83, 144.45) * mm, "radius": 2.39 * mm});
            skCircle(sketch, "E4.15.0.0", {"center": v(-2.48, 74.6) * mm, "radius": 2.39 * mm});
            skCircle(sketch, "E4.15.1.0", {"center": v(-2.48, 80.95) * mm, "radius": 2.39 * mm});
            skCircle(sketch, "E4.15.2.0", {"center": v(-2.48, 87.3) * mm, "radius": 2.39 * mm});
            skCircle(sketch, "E4.15.3.0", {"center": v(-2.48, 93.65) * mm, "radius": 2.39 * mm});
            skCircle(sketch, "E4.15.4.0", {"center": v(-2.48, 100) * mm, "radius": 2.39 * mm});
            skCircle(sketch, "E4.15.5.0", {"center": v(-2.48, 106.35) * mm, "radius": 2.39 * mm});
            skCircle(sketch, "E4.15.6.0", {"center": v(-2.48, 112.7) * mm, "radius": 2.39 * mm});
            skCircle(sketch, "E4.15.7.0", {"center": v(-2.48, 119.05) * mm, "radius": 2.39 * mm});
            skCircle(sketch, "E4.15.8.0", {"center": v(-2.48, 125.4) * mm, "radius": 2.39 * mm});
            skCircle(sketch, "E4.15.9.0", {"center": v(-2.48, 131.75) * mm, "radius": 2.39 * mm});
            skCircle(sketch, "E4.15.10.0", {"center": v(-2.48, 138.1) * mm, "radius": 2.39 * mm});
            skCircle(sketch, "E4.15.11.0", {"center": v(-2.48, 144.45) * mm, "radius": 2.39 * mm});
            skCircle(sketch, "E4.16.0.0", {"center": v(3.87, 74.6) * mm, "radius": 2.39 * mm});
            skCircle(sketch, "E4.16.1.0", {"center": v(3.87, 80.95) * mm, "radius": 2.39 * mm});
            skCircle(sketch, "E4.16.2.0", {"center": v(3.87, 87.3) * mm, "radius": 2.39 * mm});
            skCircle(sketch, "E4.16.3.0", {"center": v(3.87, 93.65) * mm, "radius": 2.39 * mm});
            skCircle(sketch, "E4.16.4.0", {"center": v(3.87, 100) * mm, "radius": 2.39 * mm});
            skCircle(sketch, "E4.16.5.0", {"center": v(3.87, 106.35) * mm, "radius": 2.39 * mm});
            skCircle(sketch, "E4.16.6.0", {"center": v(3.87, 112.7) * mm, "radius": 2.39 * mm});
            skCircle(sketch, "E4.16.7.0", {"center": v(3.87, 119.05) * mm, "radius": 2.39 * mm});
            skCircle(sketch, "E4.16.8.0", {"center": v(3.87, 125.4) * mm, "radius": 2.39 * mm});
            skCircle(sketch, "E4.16.9.0", {"center": v(3.87, 131.75) * mm, "radius": 2.39 * mm});
            skCircle(sketch, "E4.16.10.0", {"center": v(3.87, 138.1) * mm, "radius": 2.39 * mm});
            skCircle(sketch, "E4.16.11.0", {"center": v(3.87, 144.45) * mm, "radius": 2.39 * mm});
            skCircle(sketch, "E4.17.0.0", {"center": v(10.22, 74.6) * mm, "radius": 2.39 * mm});
            skCircle(sketch, "E4.17.1.0", {"center": v(10.22, 80.95) * mm, "radius": 2.39 * mm});
            skCircle(sketch, "E4.17.2.0", {"center": v(10.22, 87.3) * mm, "radius": 2.39 * mm});
            skCircle(sketch, "E4.17.3.0", {"center": v(10.22, 93.65) * mm, "radius": 2.39 * mm});
            skCircle(sketch, "E4.17.4.0", {"center": v(10.22, 100) * mm, "radius": 2.39 * mm});
            skCircle(sketch, "E4.17.5.0", {"center": v(10.22, 106.35) * mm, "radius": 2.39 * mm});
            skCircle(sketch, "E4.17.6.0", {"center": v(10.22, 112.7) * mm, "radius": 2.39 * mm});
            skCircle(sketch, "E4.17.7.0", {"center": v(10.22, 119.05) * mm, "radius": 2.39 * mm});
            skCircle(sketch, "E4.17.8.0", {"center": v(10.22, 125.4) * mm, "radius": 2.39 * mm});
            skCircle(sketch, "E4.17.9.0", {"center": v(10.22, 131.75) * mm, "radius": 2.39 * mm});
            skCircle(sketch, "E4.17.10.0", {"center": v(10.22, 138.1) * mm, "radius": 2.39 * mm});
            skCircle(sketch, "E4.17.11.0", {"center": v(10.22, 144.45) * mm, "radius": 2.39 * mm});
            skCircle(sketch, "E4.18.0.0", {"center": v(16.57, 74.6) * mm, "radius": 2.39 * mm});
            skCircle(sketch, "E4.18.1.0", {"center": v(16.57, 80.95) * mm, "radius": 2.39 * mm});
            skCircle(sketch, "E4.18.2.0", {"center": v(16.57, 87.3) * mm, "radius": 2.39 * mm});
            skCircle(sketch, "E4.18.3.0", {"center": v(16.57, 93.65) * mm, "radius": 2.39 * mm});
            skCircle(sketch, "E4.18.4.0", {"center": v(16.57, 100) * mm, "radius": 2.39 * mm});
            skCircle(sketch, "E4.18.5.0", {"center": v(16.57, 106.35) * mm, "radius": 2.39 * mm});
            skCircle(sketch, "E4.18.6.0", {"center": v(16.57, 112.7) * mm, "radius": 2.39 * mm});
            skCircle(sketch, "E4.18.7.0", {"center": v(16.57, 119.05) * mm, "radius": 2.39 * mm});
            skCircle(sketch, "E4.18.8.0", {"center": v(16.57, 125.4) * mm, "radius": 2.39 * mm});
            skCircle(sketch, "E4.18.9.0", {"center": v(16.57, 131.75) * mm, "radius": 2.39 * mm});
            skCircle(sketch, "E4.18.10.0", {"center": v(16.57, 138.1) * mm, "radius": 2.39 * mm});
            skCircle(sketch, "E4.18.11.0", {"center": v(16.57, 144.45) * mm, "radius": 2.39 * mm});
            skLineSegment(sketch, "E4.direction1", {"start": v(-97.73, 74.6) * mm, "end": v(-91.38, 74.6) * mm, "construction": true});
            skLineSegment(sketch, "E4.direction2", {"start": v(-97.73, 74.6) * mm, "end": v(-97.73, 80.95) * mm, "construction": true});
            skCircle(sketch, "E5", {"center": v(-97.73, 157.15) * mm, "radius": 2.39 * mm});
            skCircle(sketch, "E6.0.1.0", {"center": v(-97.73, 163.5) * mm, "radius": 2.39 * mm});
            skCircle(sketch, "E6.0.2.0", {"center": v(-97.73, 169.85) * mm, "radius": 2.39 * mm});
            skCircle(sketch, "E6.1.0.0", {"center": v(-91.38, 157.15) * mm, "radius": 2.39 * mm});
            skCircle(sketch, "E6.1.1.0", {"center": v(-91.38, 163.5) * mm, "radius": 2.39 * mm});
            skCircle(sketch, "E6.1.2.0", {"center": v(-91.38, 169.85) * mm, "radius": 2.39 * mm});
            skCircle(sketch, "E6.2.0.0", {"center": v(-85.03, 157.15) * mm, "radius": 2.39 * mm});
            skCircle(sketch, "E6.2.1.0", {"center": v(-85.03, 163.5) * mm, "radius": 2.39 * mm});
            skCircle(sketch, "E6.2.2.0", {"center": v(-85.03, 169.85) * mm, "radius": 2.39 * mm});
            skCircle(sketch, "E6.3.0.0", {"center": v(-78.68, 157.15) * mm, "radius": 2.39 * mm});
            skCircle(sketch, "E6.3.1.0", {"center": v(-78.68, 163.5) * mm, "radius": 2.39 * mm});
            skCircle(sketch, "E6.3.2.0", {"center": v(-78.68, 169.85) * mm, "radius": 2.39 * mm});
            skCircle(sketch, "E6.4.0.0", {"center": v(-72.33, 157.15) * mm, "radius": 2.39 * mm});
            skCircle(sketch, "E6.4.1.0", {"center": v(-72.33, 163.5) * mm, "radius": 2.39 * mm});
            skCircle(sketch, "E6.4.2.0", {"center": v(-72.33, 169.85) * mm, "radius": 2.39 * mm});
            skCircle(sketch, "E6.5.0.0", {"center": v(-65.98, 157.15) * mm, "radius": 2.39 * mm});
            skCircle(sketch, "E6.5.1.0", {"center": v(-65.98, 163.5) * mm, "radius": 2.39 * mm});
            skCircle(sketch, "E6.5.2.0", {"center": v(-65.98, 169.85) * mm, "radius": 2.39 * mm});
            skCircle(sketch, "E6.6.0.0", {"center": v(-59.63, 157.15) * mm, "radius": 2.39 * mm});
            skCircle(sketch, "E6.6.1.0", {"center": v(-59.63, 163.5) * mm, "radius": 2.39 * mm});
            skCircle(sketch, "E6.6.2.0", {"center": v(-59.63, 169.85) * mm, "radius": 2.39 * mm});
            skCircle(sketch, "E6.7.0.0", {"center": v(-53.28, 157.15) * mm, "radius": 2.39 * mm});
            skCircle(sketch, "E6.7.1.0", {"center": v(-53.28, 163.5) * mm, "radius": 2.39 * mm});
            skCircle(sketch, "E6.7.2.0", {"center": v(-53.28, 169.85) * mm, "radius": 2.39 * mm});
            skCircle(sketch, "E6.8.0.0", {"center": v(-46.93, 157.15) * mm, "radius": 2.39 * mm});
            skCircle(sketch, "E6.8.1.0", {"center": v(-46.93, 163.5) * mm, "radius": 2.39 * mm});
            skCircle(sketch, "E6.8.2.0", {"center": v(-46.93, 169.85) * mm, "radius": 2.39 * mm});
            skCircle(sketch, "E6.9.0.0", {"center": v(-40.58, 157.15) * mm, "radius": 2.39 * mm});
            skCircle(sketch, "E6.9.1.0", {"center": v(-40.58, 163.5) * mm, "radius": 2.39 * mm});
            skCircle(sketch, "E6.9.2.0", {"center": v(-40.58, 169.85) * mm, "radius": 2.39 * mm});
            skCircle(sketch, "E6.10.0.0", {"center": v(-34.23, 157.15) * mm, "radius": 2.39 * mm});
            skCircle(sketch, "E6.10.1.0", {"center": v(-34.23, 163.5) * mm, "radius": 2.39 * mm});
            skCircle(sketch, "E6.10.2.0", {"center": v(-34.23, 169.85) * mm, "radius": 2.39 * mm});
            skCircle(sketch, "E6.11.0.0", {"center": v(-27.88, 157.15) * mm, "radius": 2.39 * mm});
            skCircle(sketch, "E6.11.1.0", {"center": v(-27.88, 163.5) * mm, "radius": 2.39 * mm});
            skCircle(sketch, "E6.11.2.0", {"center": v(-27.88, 169.85) * mm, "radius": 2.39 * mm});
            skCircle(sketch, "E6.12.0.0", {"center": v(-21.53, 157.15) * mm, "radius": 2.39 * mm});
            skCircle(sketch, "E6.12.1.0", {"center": v(-21.53, 163.5) * mm, "radius": 2.39 * mm});
            skCircle(sketch, "E6.12.2.0", {"center": v(-21.53, 169.85) * mm, "radius": 2.39 * mm});
            skCircle(sketch, "E6.13.0.0", {"center": v(-15.18, 157.15) * mm, "radius": 2.39 * mm});
            skCircle(sketch, "E6.13.1.0", {"center": v(-15.18, 163.5) * mm, "radius": 2.39 * mm});
            skCircle(sketch, "E6.13.2.0", {"center": v(-15.18, 169.85) * mm, "radius": 2.39 * mm});
            skCircle(sketch, "E6.14.0.0", {"center": v(-8.83, 157.15) * mm, "radius": 2.39 * mm});
            skCircle(sketch, "E6.14.1.0", {"center": v(-8.83, 163.5) * mm, "radius": 2.39 * mm});
            skCircle(sketch, "E6.14.2.0", {"center": v(-8.83, 169.85) * mm, "radius": 2.39 * mm});
            skCircle(sketch, "E6.15.0.0", {"center": v(-2.48, 157.15) * mm, "radius": 2.39 * mm});
            skCircle(sketch, "E6.15.1.0", {"center": v(-2.48, 163.5) * mm, "radius": 2.39 * mm});
            skCircle(sketch, "E6.15.2.0", {"center": v(-2.48, 169.85) * mm, "radius": 2.39 * mm});
            skCircle(sketch, "E6.16.0.0", {"center": v(3.87, 157.15) * mm, "radius": 2.39 * mm});
            skCircle(sketch, "E6.16.1.0", {"center": v(3.87, 163.5) * mm, "radius": 2.39 * mm});
            skCircle(sketch, "E6.16.2.0", {"center": v(3.87, 169.85) * mm, "radius": 2.39 * mm});
            skCircle(sketch, "E6.17.0.0", {"center": v(10.22, 157.15) * mm, "radius": 2.39 * mm});
            skCircle(sketch, "E6.17.1.0", {"center": v(10.22, 163.5) * mm, "radius": 2.39 * mm});
            skCircle(sketch, "E6.17.2.0", {"center": v(10.22, 169.85) * mm, "radius": 2.39 * mm});
            skCircle(sketch, "E6.18.0.0", {"center": v(16.57, 157.15) * mm, "radius": 2.39 * mm});
            skCircle(sketch, "E6.18.1.0", {"center": v(16.57, 163.5) * mm, "radius": 2.39 * mm});
            skCircle(sketch, "E6.18.2.0", {"center": v(16.57, 169.85) * mm, "radius": 2.39 * mm});
            skCircle(sketch, "E6.19.0.0", {"center": v(22.92, 157.15) * mm, "radius": 2.39 * mm});
            skCircle(sketch, "E6.19.1.0", {"center": v(22.92, 163.5) * mm, "radius": 2.39 * mm});
            skCircle(sketch, "E6.19.2.0", {"center": v(22.92, 169.85) * mm, "radius": 2.39 * mm});
            skCircle(sketch, "E6.20.0.0", {"center": v(29.27, 157.15) * mm, "radius": 2.39 * mm});
            skCircle(sketch, "E6.20.1.0", {"center": v(29.27, 163.5) * mm, "radius": 2.39 * mm});
            skCircle(sketch, "E6.20.2.0", {"center": v(29.27, 169.85) * mm, "radius": 2.39 * mm});
            skCircle(sketch, "E6.21.0.0", {"center": v(35.62, 157.15) * mm, "radius": 2.39 * mm});
            skCircle(sketch, "E6.21.1.0", {"center": v(35.62, 163.5) * mm, "radius": 2.39 * mm});
            skCircle(sketch, "E6.21.2.0", {"center": v(35.62, 169.85) * mm, "radius": 2.39 * mm});
            skLineSegment(sketch, "E6.direction1", {"start": v(-97.73, 157.15) * mm, "end": v(-91.38, 157.15) * mm, "construction": true});
            skLineSegment(sketch, "E6.direction2", {"start": v(-97.73, 157.15) * mm, "end": v(-97.73, 163.5) * mm, "construction": true});
            skCircle(sketch, "E7", {"center": v(29.27, -20.65) * mm, "radius": 2.39 * mm});
            skCircle(sketch, "E8.0.1.0", {"center": v(29.27, -14.3) * mm, "radius": 2.39 * mm});
            skCircle(sketch, "E8.0.2.0", {"center": v(29.27, -7.95) * mm, "radius": 2.39 * mm});
            skCircle(sketch, "E8.0.3.0", {"center": v(29.27, -1.6) * mm, "radius": 2.39 * mm});
            skCircle(sketch, "E8.0.4.0", {"center": v(29.27, 4.75) * mm, "radius": 2.39 * mm});
            skCircle(sketch, "E8.0.5.0", {"center": v(29.27, 11.1) * mm, "radius": 2.39 * mm});
            skCircle(sketch, "E8.0.6.0", {"center": v(29.27, 17.45) * mm, "radius": 2.39 * mm});
            skCircle(sketch, "E8.0.7.0", {"center": v(29.27, 23.8) * mm, "radius": 2.39 * mm});
            skCircle(sketch, "E8.0.8.0", {"center": v(29.27, 30.15) * mm, "radius": 2.39 * mm});
            skCircle(sketch, "E8.0.9.0", {"center": v(29.27, 36.5) * mm, "radius": 2.39 * mm});
            skCircle(sketch, "E8.0.10.0", {"center": v(29.27, 42.85) * mm, "radius": 2.39 * mm});
            skCircle(sketch, "E8.0.11.0", {"center": v(29.27, 49.2) * mm, "radius": 2.39 * mm});
            skCircle(sketch, "E8.0.12.0", {"center": v(29.27, 55.55) * mm, "radius": 2.39 * mm});
            skCircle(sketch, "E8.0.13.0", {"center": v(29.27, 61.9) * mm, "radius": 2.39 * mm});
            skCircle(sketch, "E8.0.14.0", {"center": v(29.27, 68.25) * mm, "radius": 2.39 * mm});
            skCircle(sketch, "E8.0.15.0", {"center": v(29.27, 74.6) * mm, "radius": 2.39 * mm});
            skCircle(sketch, "E8.0.16.0", {"center": v(29.27, 80.95) * mm, "radius": 2.39 * mm});
            skCircle(sketch, "E8.0.17.0", {"center": v(29.27, 87.3) * mm, "radius": 2.39 * mm});
            skCircle(sketch, "E8.0.18.0", {"center": v(29.27, 93.65) * mm, "radius": 2.39 * mm});
            skCircle(sketch, "E8.0.19.0", {"center": v(29.27, 100) * mm, "radius": 2.39 * mm});
            skCircle(sketch, "E8.0.20.0", {"center": v(29.27, 106.35) * mm, "radius": 2.39 * mm});
            skCircle(sketch, "E8.0.21.0", {"center": v(29.27, 112.7) * mm, "radius": 2.39 * mm});
            skCircle(sketch, "E8.0.22.0", {"center": v(29.27, 119.05) * mm, "radius": 2.39 * mm});
            skCircle(sketch, "E8.0.23.0", {"center": v(29.27, 125.4) * mm, "radius": 2.39 * mm});
            skCircle(sketch, "E8.0.24.0", {"center": v(29.27, 131.75) * mm, "radius": 2.39 * mm});
            skCircle(sketch, "E8.0.25.0", {"center": v(29.27, 138.1) * mm, "radius": 2.39 * mm});
            skCircle(sketch, "E8.0.26.0", {"center": v(29.27, 144.45) * mm, "radius": 2.39 * mm});
            skCircle(sketch, "E8.0.27.0", {"center": v(29.27, 150.8) * mm, "radius": 2.39 * mm});
            skCircle(sketch, "E8.1.0.0", {"center": v(35.62, -20.65) * mm, "radius": 2.39 * mm});
            skCircle(sketch, "E8.1.1.0", {"center": v(35.62, -14.3) * mm, "radius": 2.39 * mm});
            skCircle(sketch, "E8.1.2.0", {"center": v(35.62, -7.95) * mm, "radius": 2.39 * mm});
            skCircle(sketch, "E8.1.3.0", {"center": v(35.62, -1.6) * mm, "radius": 2.39 * mm});
            skCircle(sketch, "E8.1.4.0", {"center": v(35.62, 4.75) * mm, "radius": 2.39 * mm});
            skCircle(sketch, "E8.1.5.0", {"center": v(35.62, 11.1) * mm, "radius": 2.39 * mm});
            skCircle(sketch, "E8.1.6.0", {"center": v(35.62, 17.45) * mm, "radius": 2.39 * mm});
            skCircle(sketch, "E8.1.7.0", {"center": v(35.62, 23.8) * mm, "radius": 2.39 * mm});
            skCircle(sketch, "E8.1.8.0", {"center": v(35.62, 30.15) * mm, "radius": 2.39 * mm});
            skCircle(sketch, "E8.1.9.0", {"center": v(35.62, 36.5) * mm, "radius": 2.39 * mm});
            skCircle(sketch, "E8.1.10.0", {"center": v(35.62, 42.85) * mm, "radius": 2.39 * mm});
            skCircle(sketch, "E8.1.11.0", {"center": v(35.62, 49.2) * mm, "radius": 2.39 * mm});
            skCircle(sketch, "E8.1.12.0", {"center": v(35.62, 55.55) * mm, "radius": 2.39 * mm});
            skCircle(sketch, "E8.1.13.0", {"center": v(35.62, 61.9) * mm, "radius": 2.39 * mm});
            skCircle(sketch, "E8.1.14.0", {"center": v(35.62, 68.25) * mm, "radius": 2.39 * mm});
            skCircle(sketch, "E8.1.15.0", {"center": v(35.62, 74.6) * mm, "radius": 2.39 * mm});
            skCircle(sketch, "E8.1.16.0", {"center": v(35.62, 80.95) * mm, "radius": 2.39 * mm});
            skCircle(sketch, "E8.1.17.0", {"center": v(35.62, 87.3) * mm, "radius": 2.39 * mm});
            skCircle(sketch, "E8.1.18.0", {"center": v(35.62, 93.65) * mm, "radius": 2.39 * mm});
            skCircle(sketch, "E8.1.19.0", {"center": v(35.62, 100) * mm, "radius": 2.39 * mm});
            skCircle(sketch, "E8.1.20.0", {"center": v(35.62, 106.35) * mm, "radius": 2.39 * mm});
            skCircle(sketch, "E8.1.21.0", {"center": v(35.62, 112.7) * mm, "radius": 2.39 * mm});
            skCircle(sketch, "E8.1.22.0", {"center": v(35.62, 119.05) * mm, "radius": 2.39 * mm});
            skCircle(sketch, "E8.1.23.0", {"center": v(35.62, 125.4) * mm, "radius": 2.39 * mm});
            skCircle(sketch, "E8.1.24.0", {"center": v(35.62, 131.75) * mm, "radius": 2.39 * mm});
            skCircle(sketch, "E8.1.25.0", {"center": v(35.62, 138.1) * mm, "radius": 2.39 * mm});
            skCircle(sketch, "E8.1.26.0", {"center": v(35.62, 144.45) * mm, "radius": 2.39 * mm});
            skCircle(sketch, "E8.1.27.0", {"center": v(35.62, 150.8) * mm, "radius": 2.39 * mm});
            skLineSegment(sketch, "E8.direction1", {"start": v(29.27, -20.65) * mm, "end": v(35.62, -20.65) * mm, "construction": true});
            skLineSegment(sketch, "E8.direction2", {"start": v(29.27, -20.65) * mm, "end": v(29.27, -14.3) * mm, "construction": true});
            skSolve(sketch);
        }
        {
            var Q0;
            Q0 = qSketchRegion(id + "F2", true);
            extrude(context, id + "F3", {"entities" : qUnion([Q0]), "operationType" : NewBodyOperationType.REMOVE, "oppositeDirection" : true, "depth" : 3.8 * mm});
        }
        {
            var Q0;
            Q0=makeQuery(id+"F3.boolean.opBoolean","COPY",FACE,{"derivedFrom":makeQuery(id+"F3.opExtrude","CAP_FACE",FACE,{"disambiguationData":[OSD([sQuery(id+"F2.wireOp",EDGE,"E1")])],"isStart":false})});
            var sketch = newSketch(context, id + "F4", { "sketchPlane" : qUnion([Q0])});
            skCircle(sketch, "E9", {"center": v(-97.73, -20.65) * mm, "radius": 0.25 * mm});
            skCircle(sketch, "E10.0.1.0", {"center": v(-97.73, -14.3) * mm, "radius": 0.25 * mm});
            skCircle(sketch, "E10.0.2.0", {"center": v(-97.73, -7.95) * mm, "radius": 0.25 * mm});
            skCircle(sketch, "E10.0.3.0", {"center": v(-97.73, -1.6) * mm, "radius": 0.25 * mm});
            skCircle(sketch, "E10.0.4.0", {"center": v(-97.73, 4.75) * mm, "radius": 0.25 * mm});
            skCircle(sketch, "E10.0.5.0", {"center": v(-97.73, 11.1) * mm, "radius": 0.25 * mm});
            skCircle(sketch, "E10.0.6.0", {"center": v(-97.73, 17.45) * mm, "radius": 0.25 * mm});
            skCircle(sketch, "E10.0.7.0", {"center": v(-97.73, 23.8) * mm, "radius": 0.25 * mm});
            skCircle(sketch, "E10.0.8.0", {"center": v(-97.73, 30.15) * mm, "radius": 0.25 * mm});
            skCircle(sketch, "E10.0.9.0", {"center": v(-97.73, 36.5) * mm, "radius": 0.25 * mm});
            skCircle(sketch, "E10.0.10.0", {"center": v(-97.73, 42.85) * mm, "radius": 0.25 * mm});
            skCircle(sketch, "E10.0.11.0", {"center": v(-97.73, 49.2) * mm, "radius": 0.25 * mm});
            skCircle(sketch, "E10.0.12.0", {"center": v(-97.73, 55.55) * mm, "radius": 0.25 * mm});
            skCircle(sketch, "E10.0.13.0", {"center": v(-97.73, 61.9) * mm, "radius": 0.25 * mm});
            skCircle(sketch, "E10.1.0.0", {"center": v(-91.38, -20.65) * mm, "radius": 0.25 * mm});
            skCircle(sketch, "E10.1.1.0", {"center": v(-91.38, -14.3) * mm, "radius": 0.25 * mm});
            skCircle(sketch, "E10.1.2.0", {"center": v(-91.38, -7.95) * mm, "radius": 0.25 * mm});
            skCircle(sketch, "E10.1.3.0", {"center": v(-91.38, -1.6) * mm, "radius": 0.25 * mm});
            skCircle(sketch, "E10.1.4.0", {"center": v(-91.38, 4.75) * mm, "radius": 0.25 * mm});
            skCircle(sketch, "E10.1.5.0", {"center": v(-91.38, 11.1) * mm, "radius": 0.25 * mm});
            skCircle(sketch, "E10.1.6.0", {"center": v(-91.38, 17.45) * mm, "radius": 0.25 * mm});
            skCircle(sketch, "E10.1.7.0", {"center": v(-91.38, 23.8) * mm, "radius": 0.25 * mm});
            skCircle(sketch, "E10.1.8.0", {"center": v(-91.38, 30.15) * mm, "radius": 0.25 * mm});
            skCircle(sketch, "E10.1.9.0", {"center": v(-91.38, 36.5) * mm, "radius": 0.25 * mm});
            skCircle(sketch, "E10.1.10.0", {"center": v(-91.38, 42.85) * mm, "radius": 0.25 * mm});
            skCircle(sketch, "E10.1.11.0", {"center": v(-91.38, 49.2) * mm, "radius": 0.25 * mm});
            skCircle(sketch, "E10.1.12.0", {"center": v(-91.38, 55.55) * mm, "radius": 0.25 * mm});
            skCircle(sketch, "E10.1.13.0", {"center": v(-91.38, 61.9) * mm, "radius": 0.25 * mm});
            skCircle(sketch, "E10.2.0.0", {"center": v(-85.03, -20.65) * mm, "radius": 0.25 * mm});
            skCircle(sketch, "E10.2.1.0", {"center": v(-85.03, -14.3) * mm, "radius": 0.25 * mm});
            skCircle(sketch, "E10.2.2.0", {"center": v(-85.03, -7.95) * mm, "radius": 0.25 * mm});
            skCircle(sketch, "E10.2.3.0", {"center": v(-85.03, -1.6) * mm, "radius": 0.25 * mm});
            skCircle(sketch, "E10.2.4.0", {"center": v(-85.03, 4.75) * mm, "radius": 0.25 * mm});
            skCircle(sketch, "E10.2.5.0", {"center": v(-85.03, 11.1) * mm, "radius": 0.25 * mm});
            skCircle(sketch, "E10.2.6.0", {"center": v(-85.03, 17.45) * mm, "radius": 0.25 * mm});
            skCircle(sketch, "E10.2.7.0", {"center": v(-85.03, 23.8) * mm, "radius": 0.25 * mm});
            skCircle(sketch, "E10.2.8.0", {"center": v(-85.03, 30.15) * mm, "radius": 0.25 * mm});
            skCircle(sketch, "E10.2.9.0", {"center": v(-85.03, 36.5) * mm, "radius": 0.25 * mm});
            skCircle(sketch, "E10.2.10.0", {"center": v(-85.03, 42.85) * mm, "radius": 0.25 * mm});
            skCircle(sketch, "E10.2.11.0", {"center": v(-85.03, 49.2) * mm, "radius": 0.25 * mm});
            skCircle(sketch, "E10.2.12.0", {"center": v(-85.03, 55.55) * mm, "radius": 0.25 * mm});
            skCircle(sketch, "E10.2.13.0", {"center": v(-85.03, 61.9) * mm, "radius": 0.25 * mm});
            skCircle(sketch, "E10.3.0.0", {"center": v(-78.68, -20.65) * mm, "radius": 0.25 * mm});
            skCircle(sketch, "E10.3.1.0", {"center": v(-78.68, -14.3) * mm, "radius": 0.25 * mm});
            skCircle(sketch, "E10.3.2.0", {"center": v(-78.68, -7.95) * mm, "radius": 0.25 * mm});
            skCircle(sketch, "E10.3.3.0", {"center": v(-78.68, -1.6) * mm, "radius": 0.25 * mm});
            skCircle(sketch, "E10.3.4.0", {"center": v(-78.68, 4.75) * mm, "radius": 0.25 * mm});
            skCircle(sketch, "E10.3.5.0", {"center": v(-78.68, 11.1) * mm, "radius": 0.25 * mm});
            skCircle(sketch, "E10.3.6.0", {"center": v(-78.68, 17.45) * mm, "radius": 0.25 * mm});
            skCircle(sketch, "E10.3.7.0", {"center": v(-78.68, 23.8) * mm, "radius": 0.25 * mm});
            skCircle(sketch, "E10.3.8.0", {"center": v(-78.68, 30.15) * mm, "radius": 0.25 * mm});
            skCircle(sketch, "E10.3.9.0", {"center": v(-78.68, 36.5) * mm, "radius": 0.25 * mm});
            skCircle(sketch, "E10.3.10.0", {"center": v(-78.68, 42.85) * mm, "radius": 0.25 * mm});
            skCircle(sketch, "E10.3.11.0", {"center": v(-78.68, 49.2) * mm, "radius": 0.25 * mm});
            skCircle(sketch, "E10.3.12.0", {"center": v(-78.68, 55.55) * mm, "radius": 0.25 * mm});
            skCircle(sketch, "E10.3.13.0", {"center": v(-78.68, 61.9) * mm, "radius": 0.25 * mm});
            skCircle(sketch, "E10.4.0.0", {"center": v(-72.33, -20.65) * mm, "radius": 0.25 * mm});
            skCircle(sketch, "E10.4.1.0", {"center": v(-72.33, -14.3) * mm, "radius": 0.25 * mm});
            skCircle(sketch, "E10.4.2.0", {"center": v(-72.33, -7.95) * mm, "radius": 0.25 * mm});
            skCircle(sketch, "E10.4.3.0", {"center": v(-72.33, -1.6) * mm, "radius": 0.25 * mm});
            skCircle(sketch, "E10.4.4.0", {"center": v(-72.33, 4.75) * mm, "radius": 0.25 * mm});
            skCircle(sketch, "E10.4.5.0", {"center": v(-72.33, 11.1) * mm, "radius": 0.25 * mm});
            skCircle(sketch, "E10.4.6.0", {"center": v(-72.33, 17.45) * mm, "radius": 0.25 * mm});
            skCircle(sketch, "E10.4.7.0", {"center": v(-72.33, 23.8) * mm, "radius": 0.25 * mm});
            skCircle(sketch, "E10.4.8.0", {"center": v(-72.33, 30.15) * mm, "radius": 0.25 * mm});
            skCircle(sketch, "E10.4.9.0", {"center": v(-72.33, 36.5) * mm, "radius": 0.25 * mm});
            skCircle(sketch, "E10.4.10.0", {"center": v(-72.33, 42.85) * mm, "radius": 0.25 * mm});
            skCircle(sketch, "E10.4.11.0", {"center": v(-72.33, 49.2) * mm, "radius": 0.25 * mm});
            skCircle(sketch, "E10.4.12.0", {"center": v(-72.33, 55.55) * mm, "radius": 0.25 * mm});
            skCircle(sketch, "E10.4.13.0", {"center": v(-72.33, 61.9) * mm, "radius": 0.25 * mm});
            skCircle(sketch, "E10.5.0.0", {"center": v(-65.98, -20.65) * mm, "radius": 0.25 * mm});
            skCircle(sketch, "E10.5.1.0", {"center": v(-65.98, -14.3) * mm, "radius": 0.25 * mm});
            skCircle(sketch, "E10.5.2.0", {"center": v(-65.98, -7.95) * mm, "radius": 0.25 * mm});
            skCircle(sketch, "E10.5.3.0", {"center": v(-65.98, -1.6) * mm, "radius": 0.25 * mm});
            skCircle(sketch, "E10.5.4.0", {"center": v(-65.98, 4.75) * mm, "radius": 0.25 * mm});
            skCircle(sketch, "E10.5.5.0", {"center": v(-65.98, 11.1) * mm, "radius": 0.25 * mm});
            skCircle(sketch, "E10.5.6.0", {"center": v(-65.98, 17.45) * mm, "radius": 0.25 * mm});
            skCircle(sketch, "E10.5.7.0", {"center": v(-65.98, 23.8) * mm, "radius": 0.25 * mm});
            skCircle(sketch, "E10.5.8.0", {"center": v(-65.98, 30.15) * mm, "radius": 0.25 * mm});
            skCircle(sketch, "E10.5.9.0", {"center": v(-65.98, 36.5) * mm, "radius": 0.25 * mm});
            skCircle(sketch, "E10.5.10.0", {"center": v(-65.98, 42.85) * mm, "radius": 0.25 * mm});
            skCircle(sketch, "E10.5.11.0", {"center": v(-65.98, 49.2) * mm, "radius": 0.25 * mm});
            skCircle(sketch, "E10.5.12.0", {"center": v(-65.98, 55.55) * mm, "radius": 0.25 * mm});
            skCircle(sketch, "E10.5.13.0", {"center": v(-65.98, 61.9) * mm, "radius": 0.25 * mm});
            skCircle(sketch, "E10.6.0.0", {"center": v(-59.63, -20.65) * mm, "radius": 0.25 * mm});
            skCircle(sketch, "E10.6.1.0", {"center": v(-59.63, -14.3) * mm, "radius": 0.25 * mm});
            skCircle(sketch, "E10.6.2.0", {"center": v(-59.63, -7.95) * mm, "radius": 0.25 * mm});
            skCircle(sketch, "E10.6.3.0", {"center": v(-59.63, -1.6) * mm, "radius": 0.25 * mm});
            skCircle(sketch, "E10.6.4.0", {"center": v(-59.63, 4.75) * mm, "radius": 0.25 * mm});
            skCircle(sketch, "E10.6.5.0", {"center": v(-59.63, 11.1) * mm, "radius": 0.25 * mm});
            skCircle(sketch, "E10.6.6.0", {"center": v(-59.63, 17.45) * mm, "radius": 0.25 * mm});
            skCircle(sketch, "E10.6.7.0", {"center": v(-59.63, 23.8) * mm, "radius": 0.25 * mm});
            skCircle(sketch, "E10.6.8.0", {"center": v(-59.63, 30.15) * mm, "radius": 0.25 * mm});
            skCircle(sketch, "E10.6.9.0", {"center": v(-59.63, 36.5) * mm, "radius": 0.25 * mm});
            skCircle(sketch, "E10.6.10.0", {"center": v(-59.63, 42.85) * mm, "radius": 0.25 * mm});
            skCircle(sketch, "E10.6.11.0", {"center": v(-59.63, 49.2) * mm, "radius": 0.25 * mm});
            skCircle(sketch, "E10.6.12.0", {"center": v(-59.63, 55.55) * mm, "radius": 0.25 * mm});
            skCircle(sketch, "E10.6.13.0", {"center": v(-59.63, 61.9) * mm, "radius": 0.25 * mm});
            skCircle(sketch, "E10.7.0.0", {"center": v(-53.28, -20.65) * mm, "radius": 0.25 * mm});
            skCircle(sketch, "E10.7.1.0", {"center": v(-53.28, -14.3) * mm, "radius": 0.25 * mm});
            skCircle(sketch, "E10.7.2.0", {"center": v(-53.28, -7.95) * mm, "radius": 0.25 * mm});
            skCircle(sketch, "E10.7.3.0", {"center": v(-53.28, -1.6) * mm, "radius": 0.25 * mm});
            skCircle(sketch, "E10.7.4.0", {"center": v(-53.28, 4.75) * mm, "radius": 0.25 * mm});
            skCircle(sketch, "E10.7.5.0", {"center": v(-53.28, 11.1) * mm, "radius": 0.25 * mm});
            skCircle(sketch, "E10.7.6.0", {"center": v(-53.28, 17.45) * mm, "radius": 0.25 * mm});
            skCircle(sketch, "E10.7.7.0", {"center": v(-53.28, 23.8) * mm, "radius": 0.25 * mm});
            skCircle(sketch, "E10.7.8.0", {"center": v(-53.28, 30.15) * mm, "radius": 0.25 * mm});
            skCircle(sketch, "E10.7.9.0", {"center": v(-53.28, 36.5) * mm, "radius": 0.25 * mm});
            skCircle(sketch, "E10.7.10.0", {"center": v(-53.28, 42.85) * mm, "radius": 0.25 * mm});
            skCircle(sketch, "E10.7.11.0", {"center": v(-53.28, 49.2) * mm, "radius": 0.25 * mm});
            skCircle(sketch, "E10.7.12.0", {"center": v(-53.28, 55.55) * mm, "radius": 0.25 * mm});
            skCircle(sketch, "E10.7.13.0", {"center": v(-53.28, 61.9) * mm, "radius": 0.25 * mm});
            skCircle(sketch, "E10.8.0.0", {"center": v(-46.93, -20.65) * mm, "radius": 0.25 * mm});
            skCircle(sketch, "E10.8.1.0", {"center": v(-46.93, -14.3) * mm, "radius": 0.25 * mm});
            skCircle(sketch, "E10.8.2.0", {"center": v(-46.93, -7.95) * mm, "radius": 0.25 * mm});
            skCircle(sketch, "E10.8.3.0", {"center": v(-46.93, -1.6) * mm, "radius": 0.25 * mm});
            skCircle(sketch, "E10.8.4.0", {"center": v(-46.93, 4.75) * mm, "radius": 0.25 * mm});
            skCircle(sketch, "E10.8.5.0", {"center": v(-46.93, 11.1) * mm, "radius": 0.25 * mm});
            skCircle(sketch, "E10.8.6.0", {"center": v(-46.93, 17.45) * mm, "radius": 0.25 * mm});
            skCircle(sketch, "E10.8.7.0", {"center": v(-46.93, 23.8) * mm, "radius": 0.25 * mm});
            skCircle(sketch, "E10.8.8.0", {"center": v(-46.93, 30.15) * mm, "radius": 0.25 * mm});
            skCircle(sketch, "E10.8.9.0", {"center": v(-46.93, 36.5) * mm, "radius": 0.25 * mm});
            skCircle(sketch, "E10.8.10.0", {"center": v(-46.93, 42.85) * mm, "radius": 0.25 * mm});
            skCircle(sketch, "E10.8.11.0", {"center": v(-46.93, 49.2) * mm, "radius": 0.25 * mm});
            skCircle(sketch, "E10.8.12.0", {"center": v(-46.93, 55.55) * mm, "radius": 0.25 * mm});
            skCircle(sketch, "E10.8.13.0", {"center": v(-46.93, 61.9) * mm, "radius": 0.25 * mm});
            skCircle(sketch, "E10.9.0.0", {"center": v(-40.58, -20.65) * mm, "radius": 0.25 * mm});
            skCircle(sketch, "E10.9.1.0", {"center": v(-40.58, -14.3) * mm, "radius": 0.25 * mm});
            skCircle(sketch, "E10.9.2.0", {"center": v(-40.58, -7.95) * mm, "radius": 0.25 * mm});
            skCircle(sketch, "E10.9.3.0", {"center": v(-40.58, -1.6) * mm, "radius": 0.25 * mm});
            skCircle(sketch, "E10.9.4.0", {"center": v(-40.58, 4.75) * mm, "radius": 0.25 * mm});
            skCircle(sketch, "E10.9.5.0", {"center": v(-40.58, 11.1) * mm, "radius": 0.25 * mm});
            skCircle(sketch, "E10.9.6.0", {"center": v(-40.58, 17.45) * mm, "radius": 0.25 * mm});
            skCircle(sketch, "E10.9.7.0", {"center": v(-40.58, 23.8) * mm, "radius": 0.25 * mm});
            skCircle(sketch, "E10.9.8.0", {"center": v(-40.58, 30.15) * mm, "radius": 0.25 * mm});
            skCircle(sketch, "E10.9.9.0", {"center": v(-40.58, 36.5) * mm, "radius": 0.25 * mm});
            skCircle(sketch, "E10.9.10.0", {"center": v(-40.58, 42.85) * mm, "radius": 0.25 * mm});
            skCircle(sketch, "E10.9.11.0", {"center": v(-40.58, 49.2) * mm, "radius": 0.25 * mm});
            skCircle(sketch, "E10.9.12.0", {"center": v(-40.58, 55.55) * mm, "radius": 0.25 * mm});
            skCircle(sketch, "E10.9.13.0", {"center": v(-40.58, 61.9) * mm, "radius": 0.25 * mm});
            skCircle(sketch, "E10.10.0.0", {"center": v(-34.23, -20.65) * mm, "radius": 0.25 * mm});
            skCircle(sketch, "E10.10.1.0", {"center": v(-34.23, -14.3) * mm, "radius": 0.25 * mm});
            skCircle(sketch, "E10.10.2.0", {"center": v(-34.23, -7.95) * mm, "radius": 0.25 * mm});
            skCircle(sketch, "E10.10.3.0", {"center": v(-34.23, -1.6) * mm, "radius": 0.25 * mm});
            skCircle(sketch, "E10.10.4.0", {"center": v(-34.23, 4.75) * mm, "radius": 0.25 * mm});
            skCircle(sketch, "E10.10.5.0", {"center": v(-34.23, 11.1) * mm, "radius": 0.25 * mm});
            skCircle(sketch, "E10.10.6.0", {"center": v(-34.23, 17.45) * mm, "radius": 0.25 * mm});
            skCircle(sketch, "E10.10.7.0", {"center": v(-34.23, 23.8) * mm, "radius": 0.25 * mm});
            skCircle(sketch, "E10.10.8.0", {"center": v(-34.23, 30.15) * mm, "radius": 0.25 * mm});
            skCircle(sketch, "E10.10.9.0", {"center": v(-34.23, 36.5) * mm, "radius": 0.25 * mm});
            skCircle(sketch, "E10.10.10.0", {"center": v(-34.23, 42.85) * mm, "radius": 0.25 * mm});
            skCircle(sketch, "E10.10.11.0", {"center": v(-34.23, 49.2) * mm, "radius": 0.25 * mm});
            skCircle(sketch, "E10.10.12.0", {"center": v(-34.23, 55.55) * mm, "radius": 0.25 * mm});
            skCircle(sketch, "E10.10.13.0", {"center": v(-34.23, 61.9) * mm, "radius": 0.25 * mm});
            skCircle(sketch, "E10.11.0.0", {"center": v(-27.88, -20.65) * mm, "radius": 0.25 * mm});
            skCircle(sketch, "E10.11.1.0", {"center": v(-27.88, -14.3) * mm, "radius": 0.25 * mm});
            skCircle(sketch, "E10.11.2.0", {"center": v(-27.88, -7.95) * mm, "radius": 0.25 * mm});
            skCircle(sketch, "E10.11.3.0", {"center": v(-27.88, -1.6) * mm, "radius": 0.25 * mm});
            skCircle(sketch, "E10.11.4.0", {"center": v(-27.88, 4.75) * mm, "radius": 0.25 * mm});
            skCircle(sketch, "E10.11.5.0", {"center": v(-27.88, 11.1) * mm, "radius": 0.25 * mm});
            skCircle(sketch, "E10.11.6.0", {"center": v(-27.88, 17.45) * mm, "radius": 0.25 * mm});
            skCircle(sketch, "E10.11.7.0", {"center": v(-27.88, 23.8) * mm, "radius": 0.25 * mm});
            skCircle(sketch, "E10.11.8.0", {"center": v(-27.88, 30.15) * mm, "radius": 0.25 * mm});
            skCircle(sketch, "E10.11.9.0", {"center": v(-27.88, 36.5) * mm, "radius": 0.25 * mm});
            skCircle(sketch, "E10.11.10.0", {"center": v(-27.88, 42.85) * mm, "radius": 0.25 * mm});
            skCircle(sketch, "E10.11.11.0", {"center": v(-27.88, 49.2) * mm, "radius": 0.25 * mm});
            skCircle(sketch, "E10.11.12.0", {"center": v(-27.88, 55.55) * mm, "radius": 0.25 * mm});
            skCircle(sketch, "E10.11.13.0", {"center": v(-27.88, 61.9) * mm, "radius": 0.25 * mm});
            skCircle(sketch, "E10.12.0.0", {"center": v(-21.53, -20.65) * mm, "radius": 0.25 * mm});
            skCircle(sketch, "E10.12.1.0", {"center": v(-21.53, -14.3) * mm, "radius": 0.25 * mm});
            skCircle(sketch, "E10.12.2.0", {"center": v(-21.53, -7.95) * mm, "radius": 0.25 * mm});
            skCircle(sketch, "E10.12.3.0", {"center": v(-21.53, -1.6) * mm, "radius": 0.25 * mm});
            skCircle(sketch, "E10.12.4.0", {"center": v(-21.53, 4.75) * mm, "radius": 0.25 * mm});
            skCircle(sketch, "E10.12.5.0", {"center": v(-21.53, 11.1) * mm, "radius": 0.25 * mm});
            skCircle(sketch, "E10.12.6.0", {"center": v(-21.53, 17.45) * mm, "radius": 0.25 * mm});
            skCircle(sketch, "E10.12.7.0", {"center": v(-21.53, 23.8) * mm, "radius": 0.25 * mm});
            skCircle(sketch, "E10.12.8.0", {"center": v(-21.53, 30.15) * mm, "radius": 0.25 * mm});
            skCircle(sketch, "E10.12.9.0", {"center": v(-21.53, 36.5) * mm, "radius": 0.25 * mm});
            skCircle(sketch, "E10.12.10.0", {"center": v(-21.53, 42.85) * mm, "radius": 0.25 * mm});
            skCircle(sketch, "E10.12.11.0", {"center": v(-21.53, 49.2) * mm, "radius": 0.25 * mm});
            skCircle(sketch, "E10.12.12.0", {"center": v(-21.53, 55.55) * mm, "radius": 0.25 * mm});
            skCircle(sketch, "E10.12.13.0", {"center": v(-21.53, 61.9) * mm, "radius": 0.25 * mm});
            skCircle(sketch, "E10.13.0.0", {"center": v(-15.18, -20.65) * mm, "radius": 0.25 * mm});
            skCircle(sketch, "E10.13.1.0", {"center": v(-15.18, -14.3) * mm, "radius": 0.25 * mm});
            skCircle(sketch, "E10.13.2.0", {"center": v(-15.18, -7.95) * mm, "radius": 0.25 * mm});
            skCircle(sketch, "E10.13.3.0", {"center": v(-15.18, -1.6) * mm, "radius": 0.25 * mm});
            skCircle(sketch, "E10.13.4.0", {"center": v(-15.18, 4.75) * mm, "radius": 0.25 * mm});
            skCircle(sketch, "E10.13.5.0", {"center": v(-15.18, 11.1) * mm, "radius": 0.25 * mm});
            skCircle(sketch, "E10.13.6.0", {"center": v(-15.18, 17.45) * mm, "radius": 0.25 * mm});
            skCircle(sketch, "E10.13.7.0", {"center": v(-15.18, 23.8) * mm, "radius": 0.25 * mm});
            skCircle(sketch, "E10.13.8.0", {"center": v(-15.18, 30.15) * mm, "radius": 0.25 * mm});
            skCircle(sketch, "E10.13.9.0", {"center": v(-15.18, 36.5) * mm, "radius": 0.25 * mm});
            skCircle(sketch, "E10.13.10.0", {"center": v(-15.18, 42.85) * mm, "radius": 0.25 * mm});
            skCircle(sketch, "E10.13.11.0", {"center": v(-15.18, 49.2) * mm, "radius": 0.25 * mm});
            skCircle(sketch, "E10.13.12.0", {"center": v(-15.18, 55.55) * mm, "radius": 0.25 * mm});
            skCircle(sketch, "E10.13.13.0", {"center": v(-15.18, 61.9) * mm, "radius": 0.25 * mm});
            skCircle(sketch, "E10.14.0.0", {"center": v(-8.83, -20.65) * mm, "radius": 0.25 * mm});
            skCircle(sketch, "E10.14.1.0", {"center": v(-8.83, -14.3) * mm, "radius": 0.25 * mm});
            skCircle(sketch, "E10.14.2.0", {"center": v(-8.83, -7.95) * mm, "radius": 0.25 * mm});
            skCircle(sketch, "E10.14.3.0", {"center": v(-8.83, -1.6) * mm, "radius": 0.25 * mm});
            skCircle(sketch, "E10.14.4.0", {"center": v(-8.83, 4.75) * mm, "radius": 0.25 * mm});
            skCircle(sketch, "E10.14.5.0", {"center": v(-8.83, 11.1) * mm, "radius": 0.25 * mm});
            skCircle(sketch, "E10.14.6.0", {"center": v(-8.83, 17.45) * mm, "radius": 0.25 * mm});
            skCircle(sketch, "E10.14.7.0", {"center": v(-8.83, 23.8) * mm, "radius": 0.25 * mm});
            skCircle(sketch, "E10.14.8.0", {"center": v(-8.83, 30.15) * mm, "radius": 0.25 * mm});
            skCircle(sketch, "E10.14.9.0", {"center": v(-8.83, 36.5) * mm, "radius": 0.25 * mm});
            skCircle(sketch, "E10.14.10.0", {"center": v(-8.83, 42.85) * mm, "radius": 0.25 * mm});
            skCircle(sketch, "E10.14.11.0", {"center": v(-8.83, 49.2) * mm, "radius": 0.25 * mm});
            skCircle(sketch, "E10.14.12.0", {"center": v(-8.83, 55.55) * mm, "radius": 0.25 * mm});
            skCircle(sketch, "E10.14.13.0", {"center": v(-8.83, 61.9) * mm, "radius": 0.25 * mm});
            skCircle(sketch, "E10.15.0.0", {"center": v(-2.48, -20.65) * mm, "radius": 0.25 * mm});
            skCircle(sketch, "E10.15.1.0", {"center": v(-2.48, -14.3) * mm, "radius": 0.25 * mm});
            skCircle(sketch, "E10.15.2.0", {"center": v(-2.48, -7.95) * mm, "radius": 0.25 * mm});
            skCircle(sketch, "E10.15.3.0", {"center": v(-2.48, -1.6) * mm, "radius": 0.25 * mm});
            skCircle(sketch, "E10.15.4.0", {"center": v(-2.48, 4.75) * mm, "radius": 0.25 * mm});
            skCircle(sketch, "E10.15.5.0", {"center": v(-2.48, 11.1) * mm, "radius": 0.25 * mm});
            skCircle(sketch, "E10.15.6.0", {"center": v(-2.48, 17.45) * mm, "radius": 0.25 * mm});
            skCircle(sketch, "E10.15.7.0", {"center": v(-2.48, 23.8) * mm, "radius": 0.25 * mm});
            skCircle(sketch, "E10.15.8.0", {"center": v(-2.48, 30.15) * mm, "radius": 0.25 * mm});
            skCircle(sketch, "E10.15.9.0", {"center": v(-2.48, 36.5) * mm, "radius": 0.25 * mm});
            skCircle(sketch, "E10.15.10.0", {"center": v(-2.48, 42.85) * mm, "radius": 0.25 * mm});
            skCircle(sketch, "E10.15.11.0", {"center": v(-2.48, 49.2) * mm, "radius": 0.25 * mm});
            skCircle(sketch, "E10.15.12.0", {"center": v(-2.48, 55.55) * mm, "radius": 0.25 * mm});
            skCircle(sketch, "E10.15.13.0", {"center": v(-2.48, 61.9) * mm, "radius": 0.25 * mm});
            skCircle(sketch, "E10.16.0.0", {"center": v(3.87, -20.65) * mm, "radius": 0.25 * mm});
            skCircle(sketch, "E10.16.1.0", {"center": v(3.87, -14.3) * mm, "radius": 0.25 * mm});
            skCircle(sketch, "E10.16.2.0", {"center": v(3.87, -7.95) * mm, "radius": 0.25 * mm});
            skCircle(sketch, "E10.16.3.0", {"center": v(3.87, -1.6) * mm, "radius": 0.25 * mm});
            skCircle(sketch, "E10.16.4.0", {"center": v(3.87, 4.75) * mm, "radius": 0.25 * mm});
            skCircle(sketch, "E10.16.5.0", {"center": v(3.87, 11.1) * mm, "radius": 0.25 * mm});
            skCircle(sketch, "E10.16.6.0", {"center": v(3.87, 17.45) * mm, "radius": 0.25 * mm});
            skCircle(sketch, "E10.16.7.0", {"center": v(3.87, 23.8) * mm, "radius": 0.25 * mm});
            skCircle(sketch, "E10.16.8.0", {"center": v(3.87, 30.15) * mm, "radius": 0.25 * mm});
            skCircle(sketch, "E10.16.9.0", {"center": v(3.87, 36.5) * mm, "radius": 0.25 * mm});
            skCircle(sketch, "E10.16.10.0", {"center": v(3.87, 42.85) * mm, "radius": 0.25 * mm});
            skCircle(sketch, "E10.16.11.0", {"center": v(3.87, 49.2) * mm, "radius": 0.25 * mm});
            skCircle(sketch, "E10.16.12.0", {"center": v(3.87, 55.55) * mm, "radius": 0.25 * mm});
            skCircle(sketch, "E10.16.13.0", {"center": v(3.87, 61.9) * mm, "radius": 0.25 * mm});
            skCircle(sketch, "E10.17.0.0", {"center": v(10.22, -20.65) * mm, "radius": 0.25 * mm});
            skCircle(sketch, "E10.17.1.0", {"center": v(10.22, -14.3) * mm, "radius": 0.25 * mm});
            skCircle(sketch, "E10.17.2.0", {"center": v(10.22, -7.95) * mm, "radius": 0.25 * mm});
            skCircle(sketch, "E10.17.3.0", {"center": v(10.22, -1.6) * mm, "radius": 0.25 * mm});
            skCircle(sketch, "E10.17.4.0", {"center": v(10.22, 4.75) * mm, "radius": 0.25 * mm});
            skCircle(sketch, "E10.17.5.0", {"center": v(10.22, 11.1) * mm, "radius": 0.25 * mm});
            skCircle(sketch, "E10.17.6.0", {"center": v(10.22, 17.45) * mm, "radius": 0.25 * mm});
            skCircle(sketch, "E10.17.7.0", {"center": v(10.22, 23.8) * mm, "radius": 0.25 * mm});
            skCircle(sketch, "E10.17.8.0", {"center": v(10.22, 30.15) * mm, "radius": 0.25 * mm});
            skCircle(sketch, "E10.17.9.0", {"center": v(10.22, 36.5) * mm, "radius": 0.25 * mm});
            skCircle(sketch, "E10.17.10.0", {"center": v(10.22, 42.85) * mm, "radius": 0.25 * mm});
            skCircle(sketch, "E10.17.11.0", {"center": v(10.22, 49.2) * mm, "radius": 0.25 * mm});
            skCircle(sketch, "E10.17.12.0", {"center": v(10.22, 55.55) * mm, "radius": 0.25 * mm});
            skCircle(sketch, "E10.17.13.0", {"center": v(10.22, 61.9) * mm, "radius": 0.25 * mm});
            skCircle(sketch, "E10.18.0.0", {"center": v(16.57, -20.65) * mm, "radius": 0.25 * mm});
            skCircle(sketch, "E10.18.1.0", {"center": v(16.57, -14.3) * mm, "radius": 0.25 * mm});
            skCircle(sketch, "E10.18.2.0", {"center": v(16.57, -7.95) * mm, "radius": 0.25 * mm});
            skCircle(sketch, "E10.18.3.0", {"center": v(16.57, -1.6) * mm, "radius": 0.25 * mm});
            skCircle(sketch, "E10.18.4.0", {"center": v(16.57, 4.75) * mm, "radius": 0.25 * mm});
            skCircle(sketch, "E10.18.5.0", {"center": v(16.57, 11.1) * mm, "radius": 0.25 * mm});
            skCircle(sketch, "E10.18.6.0", {"center": v(16.57, 17.45) * mm, "radius": 0.25 * mm});
            skCircle(sketch, "E10.18.7.0", {"center": v(16.57, 23.8) * mm, "radius": 0.25 * mm});
            skCircle(sketch, "E10.18.8.0", {"center": v(16.57, 30.15) * mm, "radius": 0.25 * mm});
            skCircle(sketch, "E10.18.9.0", {"center": v(16.57, 36.5) * mm, "radius": 0.25 * mm});
            skCircle(sketch, "E10.18.10.0", {"center": v(16.57, 42.85) * mm, "radius": 0.25 * mm});
            skCircle(sketch, "E10.18.11.0", {"center": v(16.57, 49.2) * mm, "radius": 0.25 * mm});
            skCircle(sketch, "E10.18.12.0", {"center": v(16.57, 55.55) * mm, "radius": 0.25 * mm});
            skCircle(sketch, "E10.18.13.0", {"center": v(16.57, 61.9) * mm, "radius": 0.25 * mm});
            skLineSegment(sketch, "E10.direction1", {"start": v(-97.73, -20.65) * mm, "end": v(-91.38, -20.65) * mm, "construction": true});
            skLineSegment(sketch, "E10.direction2", {"start": v(-97.73, -20.65) * mm, "end": v(-97.73, -14.3) * mm, "construction": true});
            skPoint(sketch, "E11", {"position": v(-97.73, 74.6) * mm});
            skCircle(sketch, "E12", {"center": v(-97.73, 74.6) * mm, "radius": 0.25 * mm});
            skPoint(sketch, "E13.0.1.0", {"position": v(-97.73, 80.95) * mm});
            skPoint(sketch, "E13.0.2.0", {"position": v(-97.73, 87.3) * mm});
            skPoint(sketch, "E13.0.3.0", {"position": v(-97.73, 93.65) * mm});
            skPoint(sketch, "E13.0.4.0", {"position": v(-97.73, 100) * mm});
            skPoint(sketch, "E13.0.5.0", {"position": v(-97.73, 106.35) * mm});
            skPoint(sketch, "E13.0.6.0", {"position": v(-97.73, 112.7) * mm});
            skPoint(sketch, "E13.0.7.0", {"position": v(-97.73, 119.05) * mm});
            skPoint(sketch, "E13.0.8.0", {"position": v(-97.73, 125.4) * mm});
            skPoint(sketch, "E13.0.9.0", {"position": v(-97.73, 131.75) * mm});
            skPoint(sketch, "E13.0.10.0", {"position": v(-97.73, 138.1) * mm});
            skPoint(sketch, "E13.0.11.0", {"position": v(-97.73, 144.45) * mm});
            skPoint(sketch, "E13.1.0.0", {"position": v(-91.38, 74.6) * mm});
            skPoint(sketch, "E13.1.1.0", {"position": v(-91.38, 80.95) * mm});
            skPoint(sketch, "E13.1.2.0", {"position": v(-91.38, 87.3) * mm});
            skPoint(sketch, "E13.1.3.0", {"position": v(-91.38, 93.65) * mm});
            skPoint(sketch, "E13.1.4.0", {"position": v(-91.38, 100) * mm});
            skPoint(sketch, "E13.1.5.0", {"position": v(-91.38, 106.35) * mm});
            skPoint(sketch, "E13.1.6.0", {"position": v(-91.38, 112.7) * mm});
            skPoint(sketch, "E13.1.7.0", {"position": v(-91.38, 119.05) * mm});
            skPoint(sketch, "E13.1.8.0", {"position": v(-91.38, 125.4) * mm});
            skPoint(sketch, "E13.1.9.0", {"position": v(-91.38, 131.75) * mm});
            skPoint(sketch, "E13.1.10.0", {"position": v(-91.38, 138.1) * mm});
            skPoint(sketch, "E13.1.11.0", {"position": v(-91.38, 144.45) * mm});
            skPoint(sketch, "E13.2.0.0", {"position": v(-85.03, 74.6) * mm});
            skPoint(sketch, "E13.2.1.0", {"position": v(-85.03, 80.95) * mm});
            skPoint(sketch, "E13.2.2.0", {"position": v(-85.03, 87.3) * mm});
            skPoint(sketch, "E13.2.3.0", {"position": v(-85.03, 93.65) * mm});
            skPoint(sketch, "E13.2.4.0", {"position": v(-85.03, 100) * mm});
            skPoint(sketch, "E13.2.5.0", {"position": v(-85.03, 106.35) * mm});
            skPoint(sketch, "E13.2.6.0", {"position": v(-85.03, 112.7) * mm});
            skPoint(sketch, "E13.2.7.0", {"position": v(-85.03, 119.05) * mm});
            skPoint(sketch, "E13.2.8.0", {"position": v(-85.03, 125.4) * mm});
            skPoint(sketch, "E13.2.9.0", {"position": v(-85.03, 131.75) * mm});
            skPoint(sketch, "E13.2.10.0", {"position": v(-85.03, 138.1) * mm});
            skPoint(sketch, "E13.2.11.0", {"position": v(-85.03, 144.45) * mm});
            skPoint(sketch, "E13.3.0.0", {"position": v(-78.68, 74.6) * mm});
            skPoint(sketch, "E13.3.1.0", {"position": v(-78.68, 80.95) * mm});
            skPoint(sketch, "E13.3.2.0", {"position": v(-78.68, 87.3) * mm});
            skPoint(sketch, "E13.3.3.0", {"position": v(-78.68, 93.65) * mm});
            skPoint(sketch, "E13.3.4.0", {"position": v(-78.68, 100) * mm});
            skPoint(sketch, "E13.3.5.0", {"position": v(-78.68, 106.35) * mm});
            skPoint(sketch, "E13.3.6.0", {"position": v(-78.68, 112.7) * mm});
            skPoint(sketch, "E13.3.7.0", {"position": v(-78.68, 119.05) * mm});
            skPoint(sketch, "E13.3.8.0", {"position": v(-78.68, 125.4) * mm});
            skPoint(sketch, "E13.3.9.0", {"position": v(-78.68, 131.75) * mm});
            skPoint(sketch, "E13.3.10.0", {"position": v(-78.68, 138.1) * mm});
            skPoint(sketch, "E13.3.11.0", {"position": v(-78.68, 144.45) * mm});
            skPoint(sketch, "E13.4.0.0", {"position": v(-72.33, 74.6) * mm});
            skPoint(sketch, "E13.4.1.0", {"position": v(-72.33, 80.95) * mm});
            skPoint(sketch, "E13.4.2.0", {"position": v(-72.33, 87.3) * mm});
            skPoint(sketch, "E13.4.3.0", {"position": v(-72.33, 93.65) * mm});
            skPoint(sketch, "E13.4.4.0", {"position": v(-72.33, 100) * mm});
            skPoint(sketch, "E13.4.5.0", {"position": v(-72.33, 106.35) * mm});
            skPoint(sketch, "E13.4.6.0", {"position": v(-72.33, 112.7) * mm});
            skPoint(sketch, "E13.4.7.0", {"position": v(-72.33, 119.05) * mm});
            skPoint(sketch, "E13.4.8.0", {"position": v(-72.33, 125.4) * mm});
            skPoint(sketch, "E13.4.9.0", {"position": v(-72.33, 131.75) * mm});
            skPoint(sketch, "E13.4.10.0", {"position": v(-72.33, 138.1) * mm});
            skPoint(sketch, "E13.4.11.0", {"position": v(-72.33, 144.45) * mm});
            skPoint(sketch, "E13.5.0.0", {"position": v(-65.98, 74.6) * mm});
            skPoint(sketch, "E13.5.1.0", {"position": v(-65.98, 80.95) * mm});
            skPoint(sketch, "E13.5.2.0", {"position": v(-65.98, 87.3) * mm});
            skPoint(sketch, "E13.5.3.0", {"position": v(-65.98, 93.65) * mm});
            skPoint(sketch, "E13.5.4.0", {"position": v(-65.98, 100) * mm});
            skPoint(sketch, "E13.5.5.0", {"position": v(-65.98, 106.35) * mm});
            skPoint(sketch, "E13.5.6.0", {"position": v(-65.98, 112.7) * mm});
            skPoint(sketch, "E13.5.7.0", {"position": v(-65.98, 119.05) * mm});
            skPoint(sketch, "E13.5.8.0", {"position": v(-65.98, 125.4) * mm});
            skPoint(sketch, "E13.5.9.0", {"position": v(-65.98, 131.75) * mm});
            skPoint(sketch, "E13.5.10.0", {"position": v(-65.98, 138.1) * mm});
            skPoint(sketch, "E13.5.11.0", {"position": v(-65.98, 144.45) * mm});
            skPoint(sketch, "E13.6.0.0", {"position": v(-59.63, 74.6) * mm});
            skPoint(sketch, "E13.6.1.0", {"position": v(-59.63, 80.95) * mm});
            skPoint(sketch, "E13.6.2.0", {"position": v(-59.63, 87.3) * mm});
            skPoint(sketch, "E13.6.3.0", {"position": v(-59.63, 93.65) * mm});
            skPoint(sketch, "E13.6.4.0", {"position": v(-59.63, 100) * mm});
            skPoint(sketch, "E13.6.5.0", {"position": v(-59.63, 106.35) * mm});
            skPoint(sketch, "E13.6.6.0", {"position": v(-59.63, 112.7) * mm});
            skPoint(sketch, "E13.6.7.0", {"position": v(-59.63, 119.05) * mm});
            skPoint(sketch, "E13.6.8.0", {"position": v(-59.63, 125.4) * mm});
            skPoint(sketch, "E13.6.9.0", {"position": v(-59.63, 131.75) * mm});
            skPoint(sketch, "E13.6.10.0", {"position": v(-59.63, 138.1) * mm});
            skPoint(sketch, "E13.6.11.0", {"position": v(-59.63, 144.45) * mm});
            skPoint(sketch, "E13.7.0.0", {"position": v(-53.28, 74.6) * mm});
            skPoint(sketch, "E13.7.1.0", {"position": v(-53.28, 80.95) * mm});
            skPoint(sketch, "E13.7.2.0", {"position": v(-53.28, 87.3) * mm});
            skPoint(sketch, "E13.7.3.0", {"position": v(-53.28, 93.65) * mm});
            skPoint(sketch, "E13.7.4.0", {"position": v(-53.28, 100) * mm});
            skPoint(sketch, "E13.7.5.0", {"position": v(-53.28, 106.35) * mm});
            skPoint(sketch, "E13.7.6.0", {"position": v(-53.28, 112.7) * mm});
            skPoint(sketch, "E13.7.7.0", {"position": v(-53.28, 119.05) * mm});
            skPoint(sketch, "E13.7.8.0", {"position": v(-53.28, 125.4) * mm});
            skPoint(sketch, "E13.7.9.0", {"position": v(-53.28, 131.75) * mm});
            skPoint(sketch, "E13.7.10.0", {"position": v(-53.28, 138.1) * mm});
            skPoint(sketch, "E13.7.11.0", {"position": v(-53.28, 144.45) * mm});
            skPoint(sketch, "E13.8.0.0", {"position": v(-46.93, 74.6) * mm});
            skPoint(sketch, "E13.8.1.0", {"position": v(-46.93, 80.95) * mm});
            skPoint(sketch, "E13.8.2.0", {"position": v(-46.93, 87.3) * mm});
            skPoint(sketch, "E13.8.3.0", {"position": v(-46.93, 93.65) * mm});
            skPoint(sketch, "E13.8.4.0", {"position": v(-46.93, 100) * mm});
            skPoint(sketch, "E13.8.5.0", {"position": v(-46.93, 106.35) * mm});
            skPoint(sketch, "E13.8.6.0", {"position": v(-46.93, 112.7) * mm});
            skPoint(sketch, "E13.8.7.0", {"position": v(-46.93, 119.05) * mm});
            skPoint(sketch, "E13.8.8.0", {"position": v(-46.93, 125.4) * mm});
            skPoint(sketch, "E13.8.9.0", {"position": v(-46.93, 131.75) * mm});
            skPoint(sketch, "E13.8.10.0", {"position": v(-46.93, 138.1) * mm});
            skPoint(sketch, "E13.8.11.0", {"position": v(-46.93, 144.45) * mm});
            skPoint(sketch, "E13.9.0.0", {"position": v(-40.58, 74.6) * mm});
            skPoint(sketch, "E13.9.1.0", {"position": v(-40.58, 80.95) * mm});
            skPoint(sketch, "E13.9.2.0", {"position": v(-40.58, 87.3) * mm});
            skPoint(sketch, "E13.9.3.0", {"position": v(-40.58, 93.65) * mm});
            skPoint(sketch, "E13.9.4.0", {"position": v(-40.58, 100) * mm});
            skPoint(sketch, "E13.9.5.0", {"position": v(-40.58, 106.35) * mm});
            skPoint(sketch, "E13.9.6.0", {"position": v(-40.58, 112.7) * mm});
            skPoint(sketch, "E13.9.7.0", {"position": v(-40.58, 119.05) * mm});
            skPoint(sketch, "E13.9.8.0", {"position": v(-40.58, 125.4) * mm});
            skPoint(sketch, "E13.9.9.0", {"position": v(-40.58, 131.75) * mm});
            skPoint(sketch, "E13.9.10.0", {"position": v(-40.58, 138.1) * mm});
            skPoint(sketch, "E13.9.11.0", {"position": v(-40.58, 144.45) * mm});
            skPoint(sketch, "E13.10.0.0", {"position": v(-34.23, 74.6) * mm});
            skPoint(sketch, "E13.10.1.0", {"position": v(-34.23, 80.95) * mm});
            skPoint(sketch, "E13.10.2.0", {"position": v(-34.23, 87.3) * mm});
            skPoint(sketch, "E13.10.3.0", {"position": v(-34.23, 93.65) * mm});
            skPoint(sketch, "E13.10.4.0", {"position": v(-34.23, 100) * mm});
            skPoint(sketch, "E13.10.5.0", {"position": v(-34.23, 106.35) * mm});
            skPoint(sketch, "E13.10.6.0", {"position": v(-34.23, 112.7) * mm});
            skPoint(sketch, "E13.10.7.0", {"position": v(-34.23, 119.05) * mm});
            skPoint(sketch, "E13.10.8.0", {"position": v(-34.23, 125.4) * mm});
            skPoint(sketch, "E13.10.9.0", {"position": v(-34.23, 131.75) * mm});
            skPoint(sketch, "E13.10.10.0", {"position": v(-34.23, 138.1) * mm});
            skPoint(sketch, "E13.10.11.0", {"position": v(-34.23, 144.45) * mm});
            skPoint(sketch, "E13.11.0.0", {"position": v(-27.88, 74.6) * mm});
            skPoint(sketch, "E13.11.1.0", {"position": v(-27.88, 80.95) * mm});
            skPoint(sketch, "E13.11.2.0", {"position": v(-27.88, 87.3) * mm});
            skPoint(sketch, "E13.11.3.0", {"position": v(-27.88, 93.65) * mm});
            skPoint(sketch, "E13.11.4.0", {"position": v(-27.88, 100) * mm});
            skPoint(sketch, "E13.11.5.0", {"position": v(-27.88, 106.35) * mm});
            skPoint(sketch, "E13.11.6.0", {"position": v(-27.88, 112.7) * mm});
            skPoint(sketch, "E13.11.7.0", {"position": v(-27.88, 119.05) * mm});
            skPoint(sketch, "E13.11.8.0", {"position": v(-27.88, 125.4) * mm});
            skPoint(sketch, "E13.11.9.0", {"position": v(-27.88, 131.75) * mm});
            skPoint(sketch, "E13.11.10.0", {"position": v(-27.88, 138.1) * mm});
            skPoint(sketch, "E13.11.11.0", {"position": v(-27.88, 144.45) * mm});
            skPoint(sketch, "E13.12.0.0", {"position": v(-21.53, 74.6) * mm});
            skPoint(sketch, "E13.12.1.0", {"position": v(-21.53, 80.95) * mm});
            skPoint(sketch, "E13.12.2.0", {"position": v(-21.53, 87.3) * mm});
            skPoint(sketch, "E13.12.3.0", {"position": v(-21.53, 93.65) * mm});
            skPoint(sketch, "E13.12.4.0", {"position": v(-21.53, 100) * mm});
            skPoint(sketch, "E13.12.5.0", {"position": v(-21.53, 106.35) * mm});
            skPoint(sketch, "E13.12.6.0", {"position": v(-21.53, 112.7) * mm});
            skPoint(sketch, "E13.12.7.0", {"position": v(-21.53, 119.05) * mm});
            skPoint(sketch, "E13.12.8.0", {"position": v(-21.53, 125.4) * mm});
            skPoint(sketch, "E13.12.9.0", {"position": v(-21.53, 131.75) * mm});
            skPoint(sketch, "E13.12.10.0", {"position": v(-21.53, 138.1) * mm});
            skPoint(sketch, "E13.12.11.0", {"position": v(-21.53, 144.45) * mm});
            skPoint(sketch, "E13.13.0.0", {"position": v(-15.18, 74.6) * mm});
            skPoint(sketch, "E13.13.1.0", {"position": v(-15.18, 80.95) * mm});
            skPoint(sketch, "E13.13.2.0", {"position": v(-15.18, 87.3) * mm});
            skPoint(sketch, "E13.13.3.0", {"position": v(-15.18, 93.65) * mm});
            skPoint(sketch, "E13.13.4.0", {"position": v(-15.18, 100) * mm});
            skPoint(sketch, "E13.13.5.0", {"position": v(-15.18, 106.35) * mm});
            skPoint(sketch, "E13.13.6.0", {"position": v(-15.18, 112.7) * mm});
            skPoint(sketch, "E13.13.7.0", {"position": v(-15.18, 119.05) * mm});
            skPoint(sketch, "E13.13.8.0", {"position": v(-15.18, 125.4) * mm});
            skPoint(sketch, "E13.13.9.0", {"position": v(-15.18, 131.75) * mm});
            skPoint(sketch, "E13.13.10.0", {"position": v(-15.18, 138.1) * mm});
            skPoint(sketch, "E13.13.11.0", {"position": v(-15.18, 144.45) * mm});
            skPoint(sketch, "E13.14.0.0", {"position": v(-8.83, 74.6) * mm});
            skPoint(sketch, "E13.14.1.0", {"position": v(-8.83, 80.95) * mm});
            skPoint(sketch, "E13.14.2.0", {"position": v(-8.83, 87.3) * mm});
            skPoint(sketch, "E13.14.3.0", {"position": v(-8.83, 93.65) * mm});
            skPoint(sketch, "E13.14.4.0", {"position": v(-8.83, 100) * mm});
            skPoint(sketch, "E13.14.5.0", {"position": v(-8.83, 106.35) * mm});
            skPoint(sketch, "E13.14.6.0", {"position": v(-8.83, 112.7) * mm});
            skPoint(sketch, "E13.14.7.0", {"position": v(-8.83, 119.05) * mm});
            skPoint(sketch, "E13.14.8.0", {"position": v(-8.83, 125.4) * mm});
            skPoint(sketch, "E13.14.9.0", {"position": v(-8.83, 131.75) * mm});
            skPoint(sketch, "E13.14.10.0", {"position": v(-8.83, 138.1) * mm});
            skPoint(sketch, "E13.14.11.0", {"position": v(-8.83, 144.45) * mm});
            skPoint(sketch, "E13.15.0.0", {"position": v(-2.48, 74.6) * mm});
            skPoint(sketch, "E13.15.1.0", {"position": v(-2.48, 80.95) * mm});
            skPoint(sketch, "E13.15.2.0", {"position": v(-2.48, 87.3) * mm});
            skPoint(sketch, "E13.15.3.0", {"position": v(-2.48, 93.65) * mm});
            skPoint(sketch, "E13.15.4.0", {"position": v(-2.48, 100) * mm});
            skPoint(sketch, "E13.15.5.0", {"position": v(-2.48, 106.35) * mm});
            skPoint(sketch, "E13.15.6.0", {"position": v(-2.48, 112.7) * mm});
            skPoint(sketch, "E13.15.7.0", {"position": v(-2.48, 119.05) * mm});
            skPoint(sketch, "E13.15.8.0", {"position": v(-2.48, 125.4) * mm});
            skPoint(sketch, "E13.15.9.0", {"position": v(-2.48, 131.75) * mm});
            skPoint(sketch, "E13.15.10.0", {"position": v(-2.48, 138.1) * mm});
            skPoint(sketch, "E13.15.11.0", {"position": v(-2.48, 144.45) * mm});
            skPoint(sketch, "E13.16.0.0", {"position": v(3.87, 74.6) * mm});
            skPoint(sketch, "E13.16.1.0", {"position": v(3.87, 80.95) * mm});
            skPoint(sketch, "E13.16.2.0", {"position": v(3.87, 87.3) * mm});
            skPoint(sketch, "E13.16.3.0", {"position": v(3.87, 93.65) * mm});
            skPoint(sketch, "E13.16.4.0", {"position": v(3.87, 100) * mm});
            skPoint(sketch, "E13.16.5.0", {"position": v(3.87, 106.35) * mm});
            skPoint(sketch, "E13.16.6.0", {"position": v(3.87, 112.7) * mm});
            skPoint(sketch, "E13.16.7.0", {"position": v(3.87, 119.05) * mm});
            skPoint(sketch, "E13.16.8.0", {"position": v(3.87, 125.4) * mm});
            skPoint(sketch, "E13.16.9.0", {"position": v(3.87, 131.75) * mm});
            skPoint(sketch, "E13.16.10.0", {"position": v(3.87, 138.1) * mm});
            skPoint(sketch, "E13.16.11.0", {"position": v(3.87, 144.45) * mm});
            skPoint(sketch, "E13.17.0.0", {"position": v(10.22, 74.6) * mm});
            skPoint(sketch, "E13.17.1.0", {"position": v(10.22, 80.95) * mm});
            skPoint(sketch, "E13.17.2.0", {"position": v(10.22, 87.3) * mm});
            skPoint(sketch, "E13.17.3.0", {"position": v(10.22, 93.65) * mm});
            skPoint(sketch, "E13.17.4.0", {"position": v(10.22, 100) * mm});
            skPoint(sketch, "E13.17.5.0", {"position": v(10.22, 106.35) * mm});
            skPoint(sketch, "E13.17.6.0", {"position": v(10.22, 112.7) * mm});
            skPoint(sketch, "E13.17.7.0", {"position": v(10.22, 119.05) * mm});
            skPoint(sketch, "E13.17.8.0", {"position": v(10.22, 125.4) * mm});
            skPoint(sketch, "E13.17.9.0", {"position": v(10.22, 131.75) * mm});
            skPoint(sketch, "E13.17.10.0", {"position": v(10.22, 138.1) * mm});
            skPoint(sketch, "E13.17.11.0", {"position": v(10.22, 144.45) * mm});
            skPoint(sketch, "E13.18.0.0", {"position": v(16.57, 74.6) * mm});
            skPoint(sketch, "E13.18.1.0", {"position": v(16.57, 80.95) * mm});
            skPoint(sketch, "E13.18.2.0", {"position": v(16.57, 87.3) * mm});
            skPoint(sketch, "E13.18.3.0", {"position": v(16.57, 93.65) * mm});
            skPoint(sketch, "E13.18.4.0", {"position": v(16.57, 100) * mm});
            skPoint(sketch, "E13.18.5.0", {"position": v(16.57, 106.35) * mm});
            skPoint(sketch, "E13.18.6.0", {"position": v(16.57, 112.7) * mm});
            skPoint(sketch, "E13.18.7.0", {"position": v(16.57, 119.05) * mm});
            skPoint(sketch, "E13.18.8.0", {"position": v(16.57, 125.4) * mm});
            skPoint(sketch, "E13.18.9.0", {"position": v(16.57, 131.75) * mm});
            skPoint(sketch, "E13.18.10.0", {"position": v(16.57, 138.1) * mm});
            skPoint(sketch, "E13.18.11.0", {"position": v(16.57, 144.45) * mm});
            skLineSegment(sketch, "E13.direction1", {"start": v(-97.73, 74.6) * mm, "end": v(-91.38, 74.6) * mm, "construction": true});
            skLineSegment(sketch, "E13.direction2", {"start": v(-97.73, 74.6) * mm, "end": v(-97.73, 80.95) * mm, "construction": true});
            skPoint(sketch, "E14", {"position": v(-97.73, 157.15) * mm});
            skCircle(sketch, "E15", {"center": v(-97.73, 157.15) * mm, "radius": 0.25 * mm});
            skCircle(sketch, "E16.0.1.0", {"center": v(-97.73, 163.5) * mm, "radius": 0.25 * mm});
            skCircle(sketch, "E16.0.2.0", {"center": v(-97.73, 169.85) * mm, "radius": 0.25 * mm});
            skCircle(sketch, "E16.1.0.0", {"center": v(-91.38, 157.15) * mm, "radius": 0.25 * mm});
            skCircle(sketch, "E16.1.1.0", {"center": v(-91.38, 163.5) * mm, "radius": 0.25 * mm});
            skCircle(sketch, "E16.1.2.0", {"center": v(-91.38, 169.85) * mm, "radius": 0.25 * mm});
            skCircle(sketch, "E16.2.0.0", {"center": v(-85.03, 157.15) * mm, "radius": 0.25 * mm});
            skCircle(sketch, "E16.2.1.0", {"center": v(-85.03, 163.5) * mm, "radius": 0.25 * mm});
            skCircle(sketch, "E16.2.2.0", {"center": v(-85.03, 169.85) * mm, "radius": 0.25 * mm});
            skCircle(sketch, "E16.3.0.0", {"center": v(-78.68, 157.15) * mm, "radius": 0.25 * mm});
            skCircle(sketch, "E16.3.1.0", {"center": v(-78.68, 163.5) * mm, "radius": 0.25 * mm});
            skCircle(sketch, "E16.3.2.0", {"center": v(-78.68, 169.85) * mm, "radius": 0.25 * mm});
            skCircle(sketch, "E16.4.0.0", {"center": v(-72.33, 157.15) * mm, "radius": 0.25 * mm});
            skCircle(sketch, "E16.4.1.0", {"center": v(-72.33, 163.5) * mm, "radius": 0.25 * mm});
            skCircle(sketch, "E16.4.2.0", {"center": v(-72.33, 169.85) * mm, "radius": 0.25 * mm});
            skCircle(sketch, "E16.5.0.0", {"center": v(-65.98, 157.15) * mm, "radius": 0.25 * mm});
            skCircle(sketch, "E16.5.1.0", {"center": v(-65.98, 163.5) * mm, "radius": 0.25 * mm});
            skCircle(sketch, "E16.5.2.0", {"center": v(-65.98, 169.85) * mm, "radius": 0.25 * mm});
            skCircle(sketch, "E16.6.0.0", {"center": v(-59.63, 157.15) * mm, "radius": 0.25 * mm});
            skCircle(sketch, "E16.6.1.0", {"center": v(-59.63, 163.5) * mm, "radius": 0.25 * mm});
            skCircle(sketch, "E16.6.2.0", {"center": v(-59.63, 169.85) * mm, "radius": 0.25 * mm});
            skCircle(sketch, "E16.7.0.0", {"center": v(-53.28, 157.15) * mm, "radius": 0.25 * mm});
            skCircle(sketch, "E16.7.1.0", {"center": v(-53.28, 163.5) * mm, "radius": 0.25 * mm});
            skCircle(sketch, "E16.7.2.0", {"center": v(-53.28, 169.85) * mm, "radius": 0.25 * mm});
            skCircle(sketch, "E16.8.0.0", {"center": v(-46.93, 157.15) * mm, "radius": 0.25 * mm});
            skCircle(sketch, "E16.8.1.0", {"center": v(-46.93, 163.5) * mm, "radius": 0.25 * mm});
            skCircle(sketch, "E16.8.2.0", {"center": v(-46.93, 169.85) * mm, "radius": 0.25 * mm});
            skCircle(sketch, "E16.9.0.0", {"center": v(-40.58, 157.15) * mm, "radius": 0.25 * mm});
            skCircle(sketch, "E16.9.1.0", {"center": v(-40.58, 163.5) * mm, "radius": 0.25 * mm});
            skCircle(sketch, "E16.9.2.0", {"center": v(-40.58, 169.85) * mm, "radius": 0.25 * mm});
            skCircle(sketch, "E16.10.0.0", {"center": v(-34.23, 157.15) * mm, "radius": 0.25 * mm});
            skCircle(sketch, "E16.10.1.0", {"center": v(-34.23, 163.5) * mm, "radius": 0.25 * mm});
            skCircle(sketch, "E16.10.2.0", {"center": v(-34.23, 169.85) * mm, "radius": 0.25 * mm});
            skCircle(sketch, "E16.11.0.0", {"center": v(-27.88, 157.15) * mm, "radius": 0.25 * mm});
            skCircle(sketch, "E16.11.1.0", {"center": v(-27.88, 163.5) * mm, "radius": 0.25 * mm});
            skCircle(sketch, "E16.11.2.0", {"center": v(-27.88, 169.85) * mm, "radius": 0.25 * mm});
            skCircle(sketch, "E16.12.0.0", {"center": v(-21.53, 157.15) * mm, "radius": 0.25 * mm});
            skCircle(sketch, "E16.12.1.0", {"center": v(-21.53, 163.5) * mm, "radius": 0.25 * mm});
            skCircle(sketch, "E16.12.2.0", {"center": v(-21.53, 169.85) * mm, "radius": 0.25 * mm});
            skCircle(sketch, "E16.13.0.0", {"center": v(-15.18, 157.15) * mm, "radius": 0.25 * mm});
            skCircle(sketch, "E16.13.1.0", {"center": v(-15.18, 163.5) * mm, "radius": 0.25 * mm});
            skCircle(sketch, "E16.13.2.0", {"center": v(-15.18, 169.85) * mm, "radius": 0.25 * mm});
            skCircle(sketch, "E16.14.0.0", {"center": v(-8.83, 157.15) * mm, "radius": 0.25 * mm});
            skCircle(sketch, "E16.14.1.0", {"center": v(-8.83, 163.5) * mm, "radius": 0.25 * mm});
            skCircle(sketch, "E16.14.2.0", {"center": v(-8.83, 169.85) * mm, "radius": 0.25 * mm});
            skCircle(sketch, "E16.15.0.0", {"center": v(-2.48, 157.15) * mm, "radius": 0.25 * mm});
            skCircle(sketch, "E16.15.1.0", {"center": v(-2.48, 163.5) * mm, "radius": 0.25 * mm});
            skCircle(sketch, "E16.15.2.0", {"center": v(-2.48, 169.85) * mm, "radius": 0.25 * mm});
            skCircle(sketch, "E16.16.0.0", {"center": v(3.87, 157.15) * mm, "radius": 0.25 * mm});
            skCircle(sketch, "E16.16.1.0", {"center": v(3.87, 163.5) * mm, "radius": 0.25 * mm});
            skCircle(sketch, "E16.16.2.0", {"center": v(3.87, 169.85) * mm, "radius": 0.25 * mm});
            skCircle(sketch, "E16.17.0.0", {"center": v(10.22, 157.15) * mm, "radius": 0.25 * mm});
            skCircle(sketch, "E16.17.1.0", {"center": v(10.22, 163.5) * mm, "radius": 0.25 * mm});
            skCircle(sketch, "E16.17.2.0", {"center": v(10.22, 169.85) * mm, "radius": 0.25 * mm});
            skCircle(sketch, "E16.18.0.0", {"center": v(16.57, 157.15) * mm, "radius": 0.25 * mm});
            skCircle(sketch, "E16.18.1.0", {"center": v(16.57, 163.5) * mm, "radius": 0.25 * mm});
            skCircle(sketch, "E16.18.2.0", {"center": v(16.57, 169.85) * mm, "radius": 0.25 * mm});
            skCircle(sketch, "E16.19.0.0", {"center": v(22.92, 157.15) * mm, "radius": 0.25 * mm});
            skCircle(sketch, "E16.19.1.0", {"center": v(22.92, 163.5) * mm, "radius": 0.25 * mm});
            skCircle(sketch, "E16.19.2.0", {"center": v(22.92, 169.85) * mm, "radius": 0.25 * mm});
            skCircle(sketch, "E16.20.0.0", {"center": v(29.27, 157.15) * mm, "radius": 0.25 * mm});
            skCircle(sketch, "E16.20.1.0", {"center": v(29.27, 163.5) * mm, "radius": 0.25 * mm});
            skCircle(sketch, "E16.20.2.0", {"center": v(29.27, 169.85) * mm, "radius": 0.25 * mm});
            skCircle(sketch, "E16.21.0.0", {"center": v(35.62, 157.15) * mm, "radius": 0.25 * mm});
            skCircle(sketch, "E16.21.1.0", {"center": v(35.62, 163.5) * mm, "radius": 0.25 * mm});
            skCircle(sketch, "E16.21.2.0", {"center": v(35.62, 169.85) * mm, "radius": 0.25 * mm});
            skLineSegment(sketch, "E16.direction1", {"start": v(-97.73, 157.15) * mm, "end": v(-91.38, 157.15) * mm, "construction": true});
            skLineSegment(sketch, "E16.direction2", {"start": v(-97.73, 157.15) * mm, "end": v(-97.73, 163.5) * mm, "construction": true});
            skCircle(sketch, "E17", {"center": v(29.27, -20.65) * mm, "radius": 0.25 * mm});
            skCircle(sketch, "E18.0.1.0", {"center": v(29.27, -14.3) * mm, "radius": 0.25 * mm});
            skCircle(sketch, "E18.0.2.0", {"center": v(29.27, -7.95) * mm, "radius": 0.25 * mm});
            skCircle(sketch, "E18.0.3.0", {"center": v(29.27, -1.6) * mm, "radius": 0.25 * mm});
            skCircle(sketch, "E18.0.4.0", {"center": v(29.27, 4.75) * mm, "radius": 0.25 * mm});
            skCircle(sketch, "E18.0.5.0", {"center": v(29.27, 11.1) * mm, "radius": 0.25 * mm});
            skCircle(sketch, "E18.0.6.0", {"center": v(29.27, 17.45) * mm, "radius": 0.25 * mm});
            skCircle(sketch, "E18.0.7.0", {"center": v(29.27, 23.8) * mm, "radius": 0.25 * mm});
            skCircle(sketch, "E18.0.8.0", {"center": v(29.27, 30.15) * mm, "radius": 0.25 * mm});
            skCircle(sketch, "E18.0.9.0", {"center": v(29.27, 36.5) * mm, "radius": 0.25 * mm});
            skCircle(sketch, "E18.0.10.0", {"center": v(29.27, 42.85) * mm, "radius": 0.25 * mm});
            skCircle(sketch, "E18.0.11.0", {"center": v(29.27, 49.2) * mm, "radius": 0.25 * mm});
            skCircle(sketch, "E18.0.12.0", {"center": v(29.27, 55.55) * mm, "radius": 0.25 * mm});
            skCircle(sketch, "E18.0.13.0", {"center": v(29.27, 61.9) * mm, "radius": 0.25 * mm});
            skCircle(sketch, "E18.0.14.0", {"center": v(29.27, 68.25) * mm, "radius": 0.25 * mm});
            skCircle(sketch, "E18.0.15.0", {"center": v(29.27, 74.6) * mm, "radius": 0.25 * mm});
            skCircle(sketch, "E18.0.16.0", {"center": v(29.27, 80.95) * mm, "radius": 0.25 * mm});
            skCircle(sketch, "E18.0.17.0", {"center": v(29.27, 87.3) * mm, "radius": 0.25 * mm});
            skCircle(sketch, "E18.0.18.0", {"center": v(29.27, 93.65) * mm, "radius": 0.25 * mm});
            skCircle(sketch, "E18.0.19.0", {"center": v(29.27, 100) * mm, "radius": 0.25 * mm});
            skCircle(sketch, "E18.0.20.0", {"center": v(29.27, 106.35) * mm, "radius": 0.25 * mm});
            skCircle(sketch, "E18.0.21.0", {"center": v(29.27, 112.7) * mm, "radius": 0.25 * mm});
            skCircle(sketch, "E18.0.22.0", {"center": v(29.27, 119.05) * mm, "radius": 0.25 * mm});
            skCircle(sketch, "E18.0.23.0", {"center": v(29.27, 125.4) * mm, "radius": 0.25 * mm});
            skCircle(sketch, "E18.0.24.0", {"center": v(29.27, 131.75) * mm, "radius": 0.25 * mm});
            skCircle(sketch, "E18.0.25.0", {"center": v(29.27, 138.1) * mm, "radius": 0.25 * mm});
            skCircle(sketch, "E18.0.26.0", {"center": v(29.27, 144.45) * mm, "radius": 0.25 * mm});
            skCircle(sketch, "E18.0.27.0", {"center": v(29.27, 150.8) * mm, "radius": 0.25 * mm});
            skCircle(sketch, "E18.1.0.0", {"center": v(35.62, -20.65) * mm, "radius": 0.25 * mm});
            skCircle(sketch, "E18.1.1.0", {"center": v(35.62, -14.3) * mm, "radius": 0.25 * mm});
            skCircle(sketch, "E18.1.2.0", {"center": v(35.62, -7.95) * mm, "radius": 0.25 * mm});
            skCircle(sketch, "E18.1.3.0", {"center": v(35.62, -1.6) * mm, "radius": 0.25 * mm});
            skCircle(sketch, "E18.1.4.0", {"center": v(35.62, 4.75) * mm, "radius": 0.25 * mm});
            skCircle(sketch, "E18.1.5.0", {"center": v(35.62, 11.1) * mm, "radius": 0.25 * mm});
            skCircle(sketch, "E18.1.6.0", {"center": v(35.62, 17.45) * mm, "radius": 0.25 * mm});
            skCircle(sketch, "E18.1.7.0", {"center": v(35.62, 23.8) * mm, "radius": 0.25 * mm});
            skCircle(sketch, "E18.1.8.0", {"center": v(35.62, 30.15) * mm, "radius": 0.25 * mm});
            skCircle(sketch, "E18.1.9.0", {"center": v(35.62, 36.5) * mm, "radius": 0.25 * mm});
            skCircle(sketch, "E18.1.10.0", {"center": v(35.62, 42.85) * mm, "radius": 0.25 * mm});
            skCircle(sketch, "E18.1.11.0", {"center": v(35.62, 49.2) * mm, "radius": 0.25 * mm});
            skCircle(sketch, "E18.1.12.0", {"center": v(35.62, 55.55) * mm, "radius": 0.25 * mm});
            skCircle(sketch, "E18.1.13.0", {"center": v(35.62, 61.9) * mm, "radius": 0.25 * mm});
            skCircle(sketch, "E18.1.14.0", {"center": v(35.62, 68.25) * mm, "radius": 0.25 * mm});
            skCircle(sketch, "E18.1.15.0", {"center": v(35.62, 74.6) * mm, "radius": 0.25 * mm});
            skCircle(sketch, "E18.1.16.0", {"center": v(35.62, 80.95) * mm, "radius": 0.25 * mm});
            skCircle(sketch, "E18.1.17.0", {"center": v(35.62, 87.3) * mm, "radius": 0.25 * mm});
            skCircle(sketch, "E18.1.18.0", {"center": v(35.62, 93.65) * mm, "radius": 0.25 * mm});
            skCircle(sketch, "E18.1.19.0", {"center": v(35.62, 100) * mm, "radius": 0.25 * mm});
            skCircle(sketch, "E18.1.20.0", {"center": v(35.62, 106.35) * mm, "radius": 0.25 * mm});
            skCircle(sketch, "E18.1.21.0", {"center": v(35.62, 112.7) * mm, "radius": 0.25 * mm});
            skCircle(sketch, "E18.1.22.0", {"center": v(35.62, 119.05) * mm, "radius": 0.25 * mm});
            skCircle(sketch, "E18.1.23.0", {"center": v(35.62, 125.4) * mm, "radius": 0.25 * mm});
            skCircle(sketch, "E18.1.24.0", {"center": v(35.62, 131.75) * mm, "radius": 0.25 * mm});
            skCircle(sketch, "E18.1.25.0", {"center": v(35.62, 138.1) * mm, "radius": 0.25 * mm});
            skCircle(sketch, "E18.1.26.0", {"center": v(35.62, 144.45) * mm, "radius": 0.25 * mm});
            skCircle(sketch, "E18.1.27.0", {"center": v(35.62, 150.8) * mm, "radius": 0.25 * mm});
            skLineSegment(sketch, "E18.direction1", {"start": v(29.27, -20.65) * mm, "end": v(35.62, -20.65) * mm, "construction": true});
            skLineSegment(sketch, "E18.direction2", {"start": v(29.27, -20.65) * mm, "end": v(29.27, -14.3) * mm, "construction": true});
            skSolve(sketch);
        }
        {
            var Q0;
            Q0 = qSketchRegion(id + "F4", true);
            extrude(context, id + "F5", {"entities" : qUnion([Q0]), "operationType" : NewBodyOperationType.REMOVE, "endBound" : BoundingType.THROUGH_ALL, "oppositeDirection" : true, "depth" : 25.4 * mm});
        }
    });
